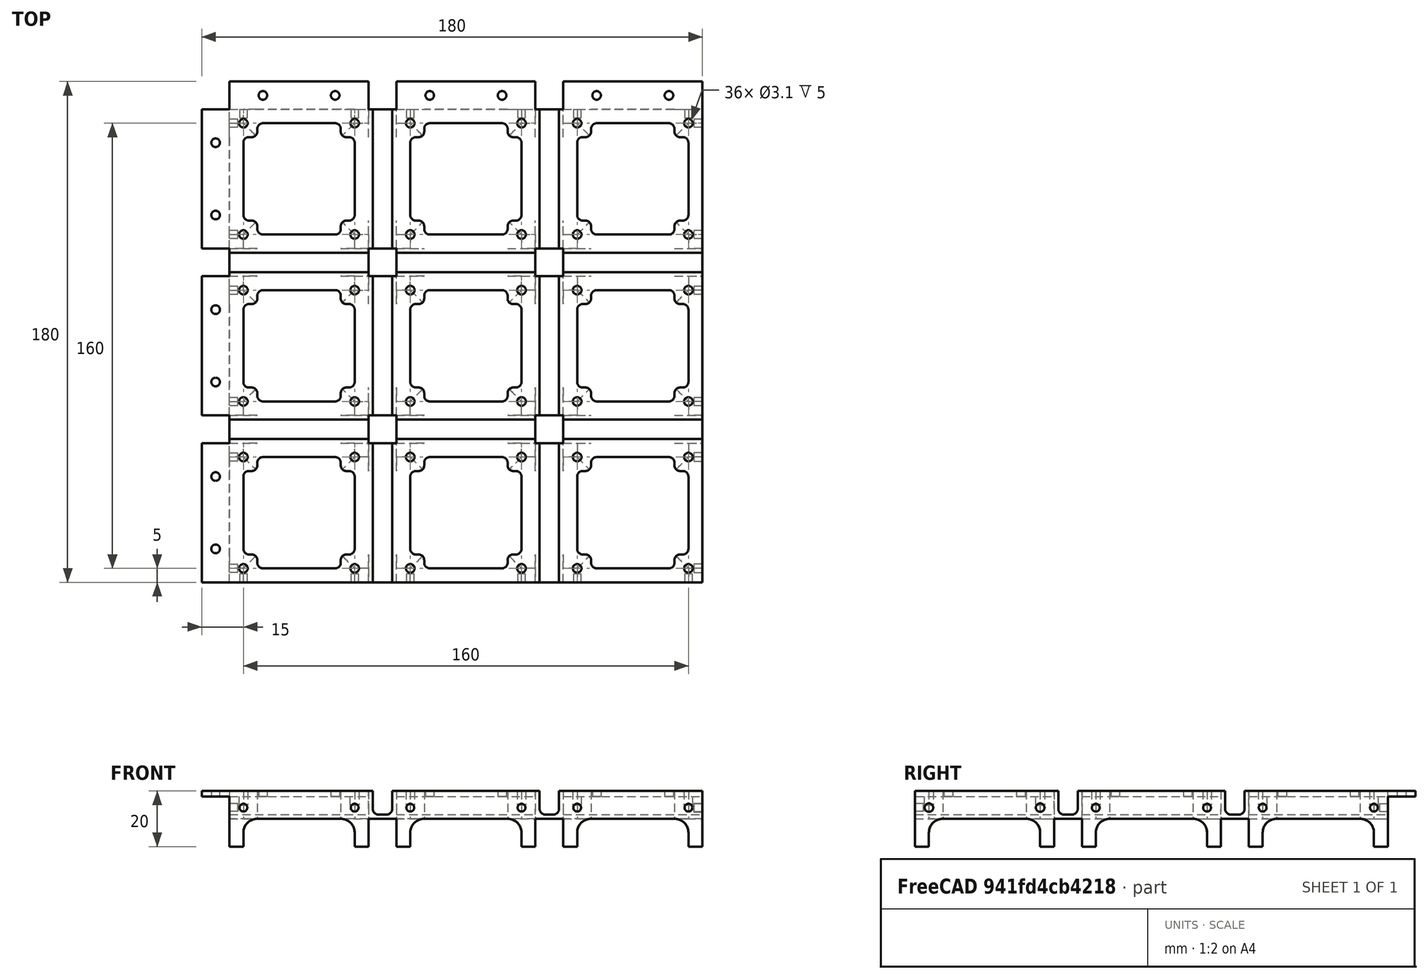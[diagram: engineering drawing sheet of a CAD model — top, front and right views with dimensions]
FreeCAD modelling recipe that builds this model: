
FCSTD DOCUMENT  (FreeCAD 0.20R29603 (Git))
Label: BackplaneRight
License: All rights reserved
LicenseURL: http://en.wikipedia.org/wiki/All_rights_reserved
objects: Sketcher::SketchObject×59, PartDesign::Pocket×49, App::Link×16, PartDesign::Pad×10, PartDesign::Body×10, Part::Cylinder×2, Part::Cut×2, Part::Box×1, App::Part×1, Part::MultiFuse×1, Mesh::Feature×1
note: 193 computed .brp shape members not serialized (recipe doc carries the construction recipe); baked Part::Feature solids carry a one-line shape summary decoded from their .brp

FEATURE [Sketcher::SketchObject] Sketch
  FullyConstrained = true
  MapMode = 5
  Placement = pos=(0,0,0) rot=(0.57735,0.57735,0.57735;2.0944rad)
  Support = -> [YZ_Plane001]
  sketch-geometry (4):
    g0: LineSegment StartX=0 StartY=0 StartZ=0 EndX=10 EndY=0 EndZ=0
    g1: LineSegment StartX=10 StartY=0 StartZ=0 EndX=10 EndY=10 EndZ=0
    g2: LineSegment StartX=10 StartY=10 StartZ=0 EndX=0 EndY=10 EndZ=0
    g3: LineSegment StartX=0 StartY=10 StartZ=0 EndX=0 EndY=0 EndZ=0
  constraints (11):
    c: Coincident(g0,g1)
    c: Coincident(g1,g2)
    c: Coincident(g2,g3)
    c: Coincident(g3,g0)
    c: Horizontal(g0)
    c: Horizontal(g2)
    c: Vertical(g1)
    c: Vertical(g3)
    c: Coincident(g0,g-1)
    c: DistanceY(g3,g3) = 10
    c: DistanceX(g2,g2) = 10
FEATURE [PartDesign::Pad] Pad
  Direction = (1,-2e-16,3e-16)
  Length = 50
  Length2 = 10
  Placement = pos=(0,0,0) rot=(0.57735,0.57735,0.57735;2.0944rad)
  Profile = -> Sketch
  ReferenceAxis = -> Sketch [N_Axis]
  Type = 0
FEATURE [Sketcher::SketchObject] Sketch001
  ExternalGeometry = -> [Pad]
  FullyConstrained = true
  MapMode = 5
  Placement = pos=(0,0,0) rot=(0.57735,0.57735,-0.57735;4.18879rad)
  Support = -> [Pad]
  sketch-geometry (6):
    g0: LineSegment StartX=8.5 StartY=-10 StartZ=0 EndX=8.5 EndY=-3.5 EndZ=0
    g1: LineSegment StartX=6.5 StartY=-1.5 StartZ=0 EndX=3.5 EndY=-1.5 EndZ=0
    g2: LineSegment StartX=1.5 StartY=-3.5 StartZ=0 EndX=1.5 EndY=-10 EndZ=0
    g3: ArcOfCircle CenterX=6.5 CenterY=-3.5 CenterZ=0 NormalX=0 NormalY=0 NormalZ=1 AngleXU=0 Radius=2 StartAngle=1e-16 EndAngle=1.5708
    g4: ArcOfCircle CenterX=3.5 CenterY=-3.5 CenterZ=0 NormalX=0 NormalY=0 NormalZ=1 AngleXU=0 Radius=2 StartAngle=1.5708 EndAngle=3.14159
    g5: LineSegment StartX=1.5 StartY=-10 StartZ=0 EndX=8.5 EndY=-10 EndZ=0
  constraints (16):
    c: PointOnObject(g0,g-3)
    c: Vertical(g0)
    c: Horizontal(g1)
    c: PointOnObject(g2,g-3)
    c: Vertical(g2)
    c: Tangent(g0,g3) = -1.5708
    c: Tangent(g1,g3) = -1.5708
    c: Tangent(g1,g4) = -1.5708
    c: Tangent(g2,g4) = -1.5708
    c: Radius(g4) = 2
    c: Radius(g3) = 2
    c: Distance(g2,g-5) = 1.5
    c: Distance(g0,g-4) = 1.5
    c: Distance(g1,g-6) = 1.5
    c: Coincident(g5,g2)
    c: Coincident(g5,g0)
FEATURE [PartDesign::Pocket] Pocket
  BaseFeature = -> Pad
  Direction = (1,-4e-16,4e-16)
  Length = 5
  Length2 = 5
  Placement = pos=(0,0,0) rot=(0.57735,0.57735,0.57735;2.0944rad)
  Profile = -> Sketch001
  ReferenceAxis = -> Sketch001 [N_Axis]
  Type = 1
FEATURE [PartDesign::Body] Body  label="BackplaneChannel"
  Group = -> [Sketch,Pad,Sketch001,Pocket]
  Origin = -> Origin001
  Placement = pos=(0,50,10) rot=(0,0,1;0rad)
  Tip = -> Pocket
FEATURE [App::Link] Link008  label="BackplaneChannel001"
  LinkPlacement = pos=(60,50,10) rot=(0,0,1;0rad)
  LinkedObject = -> Body
  Placement = pos=(60,50,10) rot=(0,0,1;0rad)
FEATURE [App::Link] Link009  label="BackplaneChannel002"
  LinkPlacement = pos=(120,50,10) rot=(0,0,1;0rad)
  LinkedObject = -> Body
  Placement = pos=(120,50,10) rot=(0,0,1;0rad)
FEATURE [App::Link] Link010  label="BackplaneChannel003"
  LinkPlacement = pos=(0,110,10) rot=(0,0,1;0rad)
  LinkedObject = -> Body
  Placement = pos=(0,110,10) rot=(0,0,1;0rad)
FEATURE [App::Link] Link011  label="BackplaneChannel004"
  LinkPlacement = pos=(60,110,10) rot=(0,0,1;0rad)
  LinkedObject = -> Body
  Placement = pos=(60,110,10) rot=(0,0,1;0rad)
FEATURE [App::Link] Link012  label="BackplaneChannel005"
  LinkPlacement = pos=(120,110,10) rot=(0,0,1;0rad)
  LinkedObject = -> Body
  Placement = pos=(120,110,10) rot=(0,0,1;0rad)
FEATURE [App::Link] Link013  label="BackplaneChannel006"
  LinkPlacement = pos=(60,0,10) rot=(0,0,1;1.5708rad)
  LinkedObject = -> Body
  Placement = pos=(60,0,10) rot=(0,0,1;1.5708rad)
FEATURE [App::Link] Link014  label="BackplaneChannel007"
  LinkPlacement = pos=(120,0,10) rot=(0,0,1;1.5708rad)
  LinkedObject = -> Body
  Placement = pos=(120,0,10) rot=(0,0,1;1.5708rad)
FEATURE [App::Link] Link015  label="BackplaneChannel008"
  LinkPlacement = pos=(60,60,10) rot=(0,0,1;1.5708rad)
  LinkedObject = -> Body
  Placement = pos=(60,60,10) rot=(0,0,1;1.5708rad)
FEATURE [App::Link] Link016  label="BackplaneChannel009"
  LinkPlacement = pos=(60,120,10) rot=(0,0,1;1.5708rad)
  LinkedObject = -> Body
  Placement = pos=(60,120,10) rot=(0,0,1;1.5708rad)
FEATURE [App::Link] Link017  label="BackplaneChannel010"
  LinkPlacement = pos=(120,60,10) rot=(0,0,1;1.5708rad)
  LinkedObject = -> Body
  Placement = pos=(120,60,10) rot=(0,0,1;1.5708rad)
FEATURE [App::Link] Link018  label="BackplaneChannel011"
  LinkPlacement = pos=(120,120,10) rot=(0,0,1;1.5708rad)
  LinkedObject = -> Body
  Placement = pos=(120,120,10) rot=(0,0,1;1.5708rad)
FEATURE [Sketcher::SketchObject] Sketch002
  FullyConstrained = true
  MapMode = 5
  Support = -> [XY_Plane002]
  sketch-geometry (4):
    g0: LineSegment StartX=-25 StartY=25 StartZ=0 EndX=25 EndY=25 EndZ=0
    g1: LineSegment StartX=25 StartY=25 StartZ=0 EndX=25 EndY=-25 EndZ=0
    g2: LineSegment StartX=25 StartY=-25 StartZ=0 EndX=-25 EndY=-25 EndZ=0
    g3: LineSegment StartX=-25 StartY=-25 StartZ=0 EndX=-25 EndY=25 EndZ=0
  constraints (10):
    c: Coincident(g0,g1)
    c: Coincident(g1,g2)
    c: Coincident(g2,g3)
    c: Coincident(g3,g0)
    c: Horizontal(g0)
    c: Vertical(g3)
    c: Symmetric(g2,g1,g-2)
    c: Symmetric(g1,g0,g-1)
    c: DistanceY(g1,g1) = 50
    c: DistanceX(g2,g2) = 50
FEATURE [PartDesign::Pad] Pad001
  Direction = (0,0,1)
  Length = 20
  Length2 = 10
  Profile = -> Sketch002
  ReferenceAxis = -> Sketch002 [N_Axis]
  Type = 0
FEATURE [Sketcher::SketchObject] Sketch003
  ExternalGeometry = -> [Pad001]
  FullyConstrained = true
  MapMode = 5
  Placement = pos=(0,0,20) rot=(0,0,1;0rad)
  Support = -> [Pad001]
  sketch-geometry (36):
    g0: LineSegment StartX=-18 StartY=15 StartZ=0 EndX=-17 EndY=15 EndZ=0
    g1: LineSegment StartX=20 StartY=13 StartZ=0 EndX=20 EndY=-13 EndZ=0
    g2: LineSegment StartX=18 StartY=-15 StartZ=0 EndX=17 EndY=-15 EndZ=0
    g3: LineSegment StartX=-20 StartY=-13 StartZ=0 EndX=-20 EndY=13 EndZ=0
    g4: LineSegment StartX=-13 StartY=20 StartZ=0 EndX=13 EndY=20 EndZ=0
    g5: LineSegment StartX=15 StartY=18 StartZ=0 EndX=15 EndY=17 EndZ=0
    g6: LineSegment StartX=13 StartY=-20 StartZ=0 EndX=-13 EndY=-20 EndZ=0
    g7: LineSegment StartX=-15 StartY=-18 StartZ=0 EndX=-15 EndY=-17 EndZ=0
    g8: LineSegment StartX=17 StartY=15 StartZ=0 EndX=18 EndY=15 EndZ=0
    g9: LineSegment StartX=-15 StartY=17 StartZ=0 EndX=-15 EndY=18 EndZ=0
    g10: LineSegment StartX=-17 StartY=-15 StartZ=0 EndX=-18 EndY=-15 EndZ=0
    g11: LineSegment StartX=15 StartY=-17 StartZ=0 EndX=15 EndY=-18 EndZ=0
    g12: ArcOfCircle CenterX=-13 CenterY=-18 CenterZ=0 NormalX=0 NormalY=0 NormalZ=1 AngleXU=0 Radius=2 StartAngle=3.14159 EndAngle=4.71239
    g13: GeomPoint X=-15 Y=-20 Z=0
    g14: ArcOfCircle CenterX=13 CenterY=-18 CenterZ=0 NormalX=0 NormalY=0 NormalZ=1 AngleXU=0 Radius=2 StartAngle=4.71239 EndAngle=6.28319
    g15: GeomPoint X=15 Y=-20 Z=0
    g16: ArcOfCircle CenterX=17 CenterY=-17 CenterZ=0 NormalX=0 NormalY=0 NormalZ=1 AngleXU=0 Radius=2 StartAngle=1.5708 EndAngle=3.14159
    g17: GeomPoint X=15 Y=-15 Z=0
    g18: ArcOfCircle CenterX=18 CenterY=-13 CenterZ=0 NormalX=0 NormalY=0 NormalZ=1 AngleXU=0 Radius=2 StartAngle=4.71239 EndAngle=6.28319
    g19: GeomPoint X=20 Y=-15 Z=0
    g20: ArcOfCircle CenterX=18 CenterY=13 CenterZ=0 NormalX=0 NormalY=0 NormalZ=1 AngleXU=0 Radius=2 StartAngle=0 EndAngle=1.5708
    g21: GeomPoint X=20 Y=15 Z=0
    g22: ArcOfCircle CenterX=17 CenterY=17 CenterZ=0 NormalX=0 NormalY=0 NormalZ=1 AngleXU=0 Radius=2 StartAngle=3.14159 EndAngle=4.71239
    g23: GeomPoint X=15 Y=15 Z=0
    g24: ArcOfCircle CenterX=13 CenterY=18 CenterZ=0 NormalX=0 NormalY=0 NormalZ=1 AngleXU=0 Radius=2 StartAngle=4e-16 EndAngle=1.5708
    g25: GeomPoint X=15 Y=20 Z=0
    g26: ArcOfCircle CenterX=-13 CenterY=18 CenterZ=0 NormalX=0 NormalY=0 NormalZ=1 AngleXU=0 Radius=2 StartAngle=1.5708 EndAngle=3.14159
    g27: GeomPoint X=-15 Y=20 Z=0
    g28: ArcOfCircle CenterX=-17 CenterY=17 CenterZ=0 NormalX=0 NormalY=0 NormalZ=1 AngleXU=0 Radius=2 StartAngle=4.71239 EndAngle=6.28319
    g29: GeomPoint X=-15 Y=15 Z=0
    g30: ArcOfCircle CenterX=-18 CenterY=13 CenterZ=0 NormalX=0 NormalY=0 NormalZ=1 AngleXU=0 Radius=2 StartAngle=1.5708 EndAngle=3.14159
    g31: GeomPoint X=-20 Y=15 Z=0
    g32: ArcOfCircle CenterX=-18 CenterY=-13 CenterZ=0 NormalX=0 NormalY=0 NormalZ=1 AngleXU=0 Radius=2 StartAngle=3.14159 EndAngle=4.71239
    g33: GeomPoint X=-20 Y=-15 Z=0
    g34: ArcOfCircle CenterX=-17 CenterY=-17 CenterZ=0 NormalX=0 NormalY=0 NormalZ=1 AngleXU=0 Radius=2 StartAngle=0 EndAngle=1.5708
    g35: GeomPoint X=-15 Y=-15 Z=0
  constraints (80):
    c: Horizontal(g2)
    c: Vertical(g3)
    c: Symmetric(g21,g31,g-2)
    c: Symmetric(g21,g19,g-1)
    c: DistanceX(g31,g21) = 40
    c: DistanceY(g19,g21) = 30
    c: Horizontal(g4)
    c: Vertical(g7)
    c: Symmetric(g13,g15,g-2)
    c: Symmetric(g15,g25,g-1)
    c: DistanceY(g15,g25) = 40
    c: Vertical(g9)
    c: Vertical(g5)
    c: Vertical(g11)
    c: Horizontal(g10)
    c: Horizontal(g8)
    c: Horizontal(g0)
    c: DistanceX(g13,g15) = 30
    c: DistanceY(g33,g31) = 30
    c: DistanceX(g27,g25) = 30
    c: PointOnObject(g13,g7)
    c: PointOnObject(g13,g6)
    c: Tangent(g7,g12) = 1.5708
    c: Tangent(g6,g12) = 1.5708
    c: Radius(g12) = 2
    c: PointOnObject(g15,g11)
    c: PointOnObject(g15,g6)
    c: Tangent(g11,g14) = 1.5708
    c: Tangent(g6,g14) = 1.5708
    c: PointOnObject(g17,g11)
    c: PointOnObject(g17,g2)
    c: Tangent(g11,g16) = -1.5708
    c: Tangent(g2,g16) = -1.5708
    c: PointOnObject(g19,g2)
    c: PointOnObject(g19,g1)
    c: Tangent(g2,g18) = 1.5708
    c: Tangent(g1,g18) = 1.5708
    c: PointOnObject(g21,g1)
    c: PointOnObject(g21,g8)
    c: Tangent(g1,g20) = 1.5708
    c: Tangent(g8,g20) = 1.5708
    c: PointOnObject(g23,g8)
    c: PointOnObject(g23,g5)
    c: Tangent(g8,g22) = -1.5708
    c: Tangent(g5,g22) = -1.5708
    c: PointOnObject(g25,g5)
    c: PointOnObject(g25,g4)
    c: Tangent(g5,g24) = 1.5708
    c: Tangent(g4,g24) = 1.5708
    c: PointOnObject(g27,g9)
    c: PointOnObject(g27,g4)
    c: Tangent(g9,g26) = 1.5708
    c: Tangent(g4,g26) = 1.5708
    c: PointOnObject(g29,g9)
    c: PointOnObject(g29,g0)
    c: Tangent(g9,g28) = -1.5708
    c: Tangent(g0,g28) = -1.5708
    c: PointOnObject(g31,g0)
    c: PointOnObject(g31,g3)
    c: Tangent(g0,g30) = 1.5708
    c: Tangent(g3,g30) = 1.5708
    c: PointOnObject(g33,g3)
    c: PointOnObject(g33,g10)
    c: Tangent(g3,g32) = 1.5708
    c: Tangent(g10,g32) = 1.5708
    c: PointOnObject(g35,g10)
    c: PointOnObject(g35,g7)
    c: Tangent(g10,g34) = -1.5708
    c: Tangent(g7,g34) = -1.5708
    c: Radius(g34) = 2
    c: Radius(g32) = 2
    c: Radius(g30) = 2
    c: Radius(g28) = 2
    c: Radius(g26) = 2
    c: Radius(g24) = 2
    c: Radius(g22) = 2
    c: Radius(g20) = 2
    c: Radius(g18) = 2
    c: Radius(g16) = 2
    c: Radius(g14) = 2
FEATURE [PartDesign::Pocket] Pocket001
  BaseFeature = -> Pad001
  Direction = (0,0,-1)
  Length = 5
  Length2 = 5
  Profile = -> Sketch003
  ReferenceAxis = -> Sketch003 [N_Axis]
  Type = 1
FEATURE [Sketcher::SketchObject] Sketch004
  ExternalGeometry = -> [Pocket001]
  FullyConstrained = true
  MapMode = 5
  Placement = pos=(25,0,0) rot=(0.57735,0.57735,0.57735;2.0944rad)
  Support = -> [Pocket001]
  sketch-geometry (6):
    g0: LineSegment StartX=-15 StartY=10 StartZ=0 EndX=15 EndY=10 EndZ=0
    g1: LineSegment StartX=20 StartY=5 StartZ=0 EndX=20 EndY=0 EndZ=0
    g2: LineSegment StartX=20 StartY=0 StartZ=0 EndX=-20 EndY=0 EndZ=0
    g3: LineSegment StartX=-20 StartY=0 StartZ=0 EndX=-20 EndY=5 EndZ=0
    g4: ArcOfCircle CenterX=15 CenterY=5 CenterZ=0 NormalX=0 NormalY=0 NormalZ=1 AngleXU=0 Radius=5 StartAngle=1.11001e-11 EndAngle=1.5708
    g5: ArcOfCircle CenterX=-15 CenterY=5 CenterZ=0 NormalX=0 NormalY=0 NormalZ=1 AngleXU=0 Radius=5 StartAngle=1.5708 EndAngle=3.14159
  constraints (15):
    c: Coincident(g1,g2)
    c: Coincident(g2,g3)
    c: Vertical(g1)
    c: Vertical(g3)
    c: PointOnObject(g1,g-1)
    c: Tangent(g1,g4) = 1.5708
    c: Tangent(g0,g4) = 1.5708
    c: Tangent(g0,g5) = 1.5708
    c: Tangent(g3,g5) = 1.5708
    c: Horizontal(g0)
    c: DistanceX(g2,g2) = 40
    c: Symmetric(g2,g1,g-2)
    c: Distance(g-1,g0) = 10
    c: Radius(g5) = 5
    c: Radius(g4) = 5
FEATURE [PartDesign::Pocket] Pocket002
  BaseFeature = -> Pocket001
  Direction = (-1,0,0)
  Length = 5
  Length2 = 5
  Profile = -> Sketch004
  ReferenceAxis = -> Sketch004 [N_Axis]
  Type = 1
FEATURE [Sketcher::SketchObject] Sketch005
  FullyConstrained = true
  MapMode = 5
  Placement = pos=(0,-25,0) rot=(1,0,0;1.5708rad)
  Support = -> [Pocket001]
  sketch-geometry (6):
    g0: LineSegment StartX=-15 StartY=10 StartZ=0 EndX=15 EndY=10 EndZ=0
    g1: LineSegment StartX=20 StartY=5 StartZ=0 EndX=20 EndY=0 EndZ=0
    g2: LineSegment StartX=20 StartY=0 StartZ=0 EndX=-20 EndY=0 EndZ=0
    g3: LineSegment StartX=-20 StartY=0 StartZ=0 EndX=-20 EndY=5 EndZ=0
    g4: ArcOfCircle CenterX=15 CenterY=5 CenterZ=0 NormalX=0 NormalY=0 NormalZ=1 AngleXU=0 Radius=5 StartAngle=1.11e-11 EndAngle=1.5708
    g5: ArcOfCircle CenterX=-15 CenterY=5 CenterZ=0 NormalX=0 NormalY=0 NormalZ=1 AngleXU=0 Radius=5 StartAngle=1.5708 EndAngle=3.14159
  constraints (15):
    c: Coincident(g1,g2)
    c: Coincident(g2,g3)
    c: Horizontal(g0)
    c: Vertical(g1)
    c: Vertical(g3)
    c: Symmetric(g2,g1,g-2)
    c: PointOnObject(g1,g-1)
    c: Tangent(g0,g4) = 1.5708
    c: Tangent(g1,g4) = 1.5708
    c: Tangent(g0,g5) = 1.5708
    c: Tangent(g3,g5) = 1.5708
    c: DistanceX(g2,g2) = 40
    c: Distance(g-1,g0) = 10
    c: Radius(g5) = 5
    c: Radius(g4) = 5
FEATURE [PartDesign::Pocket] Pocket003
  BaseFeature = -> Pocket002
  Direction = (0,1,-2e-16)
  Length = 5
  Length2 = 5
  Profile = -> Sketch005
  ReferenceAxis = -> Sketch005 [N_Axis]
  Type = 1
FEATURE [Sketcher::SketchObject] Sketch009
  FullyConstrained = false
  MapMode = 5
  Placement = pos=(0,0,20) rot=(0,0,1;0rad)
  sketch-geometry (4):
    g0: Circle CenterX=-20 CenterY=20 CenterZ=0 NormalX=0 NormalY=0 NormalZ=1 AngleXU=0 Radius=1.55
    g1: Circle CenterX=20 CenterY=20 CenterZ=0 NormalX=0 NormalY=0 NormalZ=1 AngleXU=0 Radius=1.55
    g2: Circle CenterX=20 CenterY=-20 CenterZ=0 NormalX=0 NormalY=0 NormalZ=1 AngleXU=0 Radius=1.55
    g3: Circle CenterX=-20 CenterY=-20 CenterZ=0 NormalX=0 NormalY=0 NormalZ=1 AngleXU=0 Radius=1.55
  constraints (4):
    c: Diameter(g0) = 3.1
    c: Diameter(g1) = 3.1
    c: Diameter(g2) = 3.1
    c: Diameter(g3) = 3.1
FEATURE [PartDesign::Pocket] Pocket008
  BaseFeature = -> Pocket003
  Direction = (0,0,-1)
  Length = 5
  Length2 = 5
  Profile = -> Sketch009
  ReferenceAxis = -> Sketch009 [N_Axis]
  Type = 0
FEATURE [Sketcher::SketchObject] Sketch010
  FullyConstrained = true
  MapMode = 5
  Support = -> [XY_Plane003]
  sketch-geometry (4):
    g0: LineSegment StartX=-25 StartY=25 StartZ=0 EndX=25 EndY=25 EndZ=0
    g1: LineSegment StartX=25 StartY=25 StartZ=0 EndX=25 EndY=-25 EndZ=0
    g2: LineSegment StartX=25 StartY=-25 StartZ=0 EndX=-25 EndY=-25 EndZ=0
    g3: LineSegment StartX=-25 StartY=-25 StartZ=0 EndX=-25 EndY=25 EndZ=0
  constraints (10):
    c: Coincident(g0,g1)
    c: Coincident(g1,g2)
    c: Coincident(g2,g3)
    c: Coincident(g3,g0)
    c: Horizontal(g0)
    c: Vertical(g3)
    c: Symmetric(g2,g1,g-2)
    c: Symmetric(g1,g0,g-1)
    c: DistanceY(g1,g1) = 50
    c: DistanceX(g2,g2) = 50
FEATURE [PartDesign::Pad] Pad002
  Direction = (0,0,1)
  Length = 20
  Length2 = 10
  Profile = -> Sketch010
  ReferenceAxis = -> Sketch010 [N_Axis]
  Type = 0
FEATURE [Sketcher::SketchObject] Sketch011
  ExternalGeometry = -> [Pad002]
  FullyConstrained = true
  MapMode = 5
  Placement = pos=(0,0,20) rot=(0,0,1;0rad)
  Support = -> [Pad002]
  sketch-geometry (36):
    g0: LineSegment StartX=-18 StartY=15 StartZ=0 EndX=-17 EndY=15 EndZ=0
    g1: LineSegment StartX=20 StartY=13 StartZ=0 EndX=20 EndY=-13 EndZ=0
    g2: LineSegment StartX=18 StartY=-15 StartZ=0 EndX=17 EndY=-15 EndZ=0
    g3: LineSegment StartX=-20 StartY=-13 StartZ=0 EndX=-20 EndY=13 EndZ=0
    g4: LineSegment StartX=-13 StartY=20 StartZ=0 EndX=13 EndY=20 EndZ=0
    g5: LineSegment StartX=15 StartY=18 StartZ=0 EndX=15 EndY=17 EndZ=0
    g6: LineSegment StartX=13 StartY=-20 StartZ=0 EndX=-13 EndY=-20 EndZ=0
    g7: LineSegment StartX=-15 StartY=-18 StartZ=0 EndX=-15 EndY=-17 EndZ=0
    g8: LineSegment StartX=17 StartY=15 StartZ=0 EndX=18 EndY=15 EndZ=0
    g9: LineSegment StartX=-15 StartY=17 StartZ=0 EndX=-15 EndY=18 EndZ=0
    g10: LineSegment StartX=-17 StartY=-15 StartZ=0 EndX=-18 EndY=-15 EndZ=0
    g11: LineSegment StartX=15 StartY=-17 StartZ=0 EndX=15 EndY=-18 EndZ=0
    g12: ArcOfCircle CenterX=-13 CenterY=-18 CenterZ=0 NormalX=0 NormalY=0 NormalZ=1 AngleXU=0 Radius=2 StartAngle=3.14159 EndAngle=4.71239
    g13: GeomPoint X=-15 Y=-20 Z=0
    g14: ArcOfCircle CenterX=13 CenterY=-18 CenterZ=0 NormalX=0 NormalY=0 NormalZ=1 AngleXU=0 Radius=2 StartAngle=4.71239 EndAngle=6.28319
    g15: GeomPoint X=15 Y=-20 Z=0
    g16: ArcOfCircle CenterX=17 CenterY=-17 CenterZ=0 NormalX=0 NormalY=0 NormalZ=1 AngleXU=0 Radius=2 StartAngle=1.5708 EndAngle=3.14159
    g17: GeomPoint X=15 Y=-15 Z=0
    g18: ArcOfCircle CenterX=18 CenterY=-13 CenterZ=0 NormalX=0 NormalY=0 NormalZ=1 AngleXU=0 Radius=2 StartAngle=4.71239 EndAngle=6.28319
    g19: GeomPoint X=20 Y=-15 Z=0
    g20: ArcOfCircle CenterX=18 CenterY=13 CenterZ=0 NormalX=0 NormalY=0 NormalZ=1 AngleXU=0 Radius=2 StartAngle=0 EndAngle=1.5708
    g21: GeomPoint X=20 Y=15 Z=0
    g22: ArcOfCircle CenterX=17 CenterY=17 CenterZ=0 NormalX=0 NormalY=0 NormalZ=1 AngleXU=0 Radius=2 StartAngle=3.14159 EndAngle=4.71239
    g23: GeomPoint X=15 Y=15 Z=0
    g24: ArcOfCircle CenterX=13 CenterY=18 CenterZ=0 NormalX=0 NormalY=0 NormalZ=1 AngleXU=0 Radius=2 StartAngle=4e-16 EndAngle=1.5708
    g25: GeomPoint X=15 Y=20 Z=0
    g26: ArcOfCircle CenterX=-13 CenterY=18 CenterZ=0 NormalX=0 NormalY=0 NormalZ=1 AngleXU=0 Radius=2 StartAngle=1.5708 EndAngle=3.14159
    g27: GeomPoint X=-15 Y=20 Z=0
    g28: ArcOfCircle CenterX=-17 CenterY=17 CenterZ=0 NormalX=0 NormalY=0 NormalZ=1 AngleXU=0 Radius=2 StartAngle=4.71239 EndAngle=6.28319
    g29: GeomPoint X=-15 Y=15 Z=0
    g30: ArcOfCircle CenterX=-18 CenterY=13 CenterZ=0 NormalX=0 NormalY=0 NormalZ=1 AngleXU=0 Radius=2 StartAngle=1.5708 EndAngle=3.14159
    g31: GeomPoint X=-20 Y=15 Z=0
    g32: ArcOfCircle CenterX=-18 CenterY=-13 CenterZ=0 NormalX=0 NormalY=0 NormalZ=1 AngleXU=0 Radius=2 StartAngle=3.14159 EndAngle=4.71239
    g33: GeomPoint X=-20 Y=-15 Z=0
    g34: ArcOfCircle CenterX=-17 CenterY=-17 CenterZ=0 NormalX=0 NormalY=0 NormalZ=1 AngleXU=0 Radius=2 StartAngle=0 EndAngle=1.5708
    g35: GeomPoint X=-15 Y=-15 Z=0
  constraints (80):
    c: Horizontal(g2)
    c: Vertical(g3)
    c: Symmetric(g21,g31,g-2)
    c: Symmetric(g21,g19,g-1)
    c: DistanceX(g31,g21) = 40
    c: DistanceY(g19,g21) = 30
    c: Horizontal(g4)
    c: Vertical(g7)
    c: Symmetric(g13,g15,g-2)
    c: Symmetric(g15,g25,g-1)
    c: DistanceY(g15,g25) = 40
    c: Vertical(g9)
    c: Vertical(g5)
    c: Vertical(g11)
    c: Horizontal(g10)
    c: Horizontal(g8)
    c: Horizontal(g0)
    c: DistanceX(g13,g15) = 30
    c: DistanceY(g33,g31) = 30
    c: DistanceX(g27,g25) = 30
    c: PointOnObject(g13,g7)
    c: PointOnObject(g13,g6)
    c: Tangent(g7,g12) = 1.5708
    c: Tangent(g6,g12) = 1.5708
    c: Radius(g12) = 2
    c: PointOnObject(g15,g11)
    c: PointOnObject(g15,g6)
    c: Tangent(g11,g14) = 1.5708
    c: Tangent(g6,g14) = 1.5708
    c: PointOnObject(g17,g11)
    c: PointOnObject(g17,g2)
    c: Tangent(g11,g16) = -1.5708
    c: Tangent(g2,g16) = -1.5708
    c: PointOnObject(g19,g2)
    c: PointOnObject(g19,g1)
    c: Tangent(g2,g18) = 1.5708
    c: Tangent(g1,g18) = 1.5708
    c: PointOnObject(g21,g1)
    c: PointOnObject(g21,g8)
    c: Tangent(g1,g20) = 1.5708
    c: Tangent(g8,g20) = 1.5708
    c: PointOnObject(g23,g8)
    c: PointOnObject(g23,g5)
    c: Tangent(g8,g22) = -1.5708
    c: Tangent(g5,g22) = -1.5708
    c: PointOnObject(g25,g5)
    c: PointOnObject(g25,g4)
    c: Tangent(g5,g24) = 1.5708
    c: Tangent(g4,g24) = 1.5708
    c: PointOnObject(g27,g9)
    c: PointOnObject(g27,g4)
    c: Tangent(g9,g26) = 1.5708
    c: Tangent(g4,g26) = 1.5708
    c: PointOnObject(g29,g9)
    c: PointOnObject(g29,g0)
    c: Tangent(g9,g28) = -1.5708
    c: Tangent(g0,g28) = -1.5708
    c: PointOnObject(g31,g0)
    c: PointOnObject(g31,g3)
    c: Tangent(g0,g30) = 1.5708
    c: Tangent(g3,g30) = 1.5708
    c: PointOnObject(g33,g3)
    c: PointOnObject(g33,g10)
    c: Tangent(g3,g32) = 1.5708
    c: Tangent(g10,g32) = 1.5708
    c: PointOnObject(g35,g10)
    c: PointOnObject(g35,g7)
    c: Tangent(g10,g34) = -1.5708
    c: Tangent(g7,g34) = -1.5708
    c: Radius(g34) = 2
    c: Radius(g32) = 2
    c: Radius(g30) = 2
    c: Radius(g28) = 2
    c: Radius(g26) = 2
    c: Radius(g24) = 2
    c: Radius(g22) = 2
    c: Radius(g20) = 2
    c: Radius(g18) = 2
    c: Radius(g16) = 2
    c: Radius(g14) = 2
FEATURE [PartDesign::Pocket] Pocket009
  BaseFeature = -> Pad002
  Direction = (0,0,-1)
  Length = 5
  Length2 = 5
  Profile = -> Sketch011
  ReferenceAxis = -> Sketch011 [N_Axis]
  Type = 1
FEATURE [Sketcher::SketchObject] Sketch012
  ExternalGeometry = -> [Pocket009]
  FullyConstrained = true
  MapMode = 5
  Placement = pos=(25,0,0) rot=(0.57735,0.57735,0.57735;2.0944rad)
  Support = -> [Pocket009]
  sketch-geometry (6):
    g0: LineSegment StartX=-15 StartY=10 StartZ=0 EndX=15 EndY=10 EndZ=0
    g1: LineSegment StartX=20 StartY=5 StartZ=0 EndX=20 EndY=0 EndZ=0
    g2: LineSegment StartX=20 StartY=0 StartZ=0 EndX=-20 EndY=0 EndZ=0
    g3: LineSegment StartX=-20 StartY=0 StartZ=0 EndX=-20 EndY=5 EndZ=0
    g4: ArcOfCircle CenterX=15 CenterY=5 CenterZ=0 NormalX=0 NormalY=0 NormalZ=1 AngleXU=0 Radius=5 StartAngle=1.11001e-11 EndAngle=1.5708
    g5: ArcOfCircle CenterX=-15 CenterY=5 CenterZ=0 NormalX=0 NormalY=0 NormalZ=1 AngleXU=0 Radius=5 StartAngle=1.5708 EndAngle=3.14159
  constraints (15):
    c: Coincident(g1,g2)
    c: Coincident(g2,g3)
    c: Vertical(g1)
    c: Vertical(g3)
    c: PointOnObject(g1,g-1)
    c: Tangent(g1,g4) = 1.5708
    c: Tangent(g0,g4) = 1.5708
    c: Tangent(g0,g5) = 1.5708
    c: Tangent(g3,g5) = 1.5708
    c: Horizontal(g0)
    c: DistanceX(g2,g2) = 40
    c: Symmetric(g2,g1,g-2)
    c: Distance(g-1,g0) = 10
    c: Radius(g5) = 5
    c: Radius(g4) = 5
FEATURE [PartDesign::Pocket] Pocket010
  BaseFeature = -> Pocket009
  Direction = (-1,0,0)
  Length = 5
  Length2 = 5
  Profile = -> Sketch012
  ReferenceAxis = -> Sketch012 [N_Axis]
  Type = 1
FEATURE [Sketcher::SketchObject] Sketch013
  FullyConstrained = true
  MapMode = 5
  Placement = pos=(0,-25,0) rot=(1,0,0;1.5708rad)
  Support = -> [Pocket009]
  sketch-geometry (6):
    g0: LineSegment StartX=-15 StartY=10 StartZ=0 EndX=15 EndY=10 EndZ=0
    g1: LineSegment StartX=20 StartY=5 StartZ=0 EndX=20 EndY=0 EndZ=0
    g2: LineSegment StartX=20 StartY=0 StartZ=0 EndX=-20 EndY=0 EndZ=0
    g3: LineSegment StartX=-20 StartY=0 StartZ=0 EndX=-20 EndY=5 EndZ=0
    g4: ArcOfCircle CenterX=15 CenterY=5 CenterZ=0 NormalX=0 NormalY=0 NormalZ=1 AngleXU=0 Radius=5 StartAngle=1.11e-11 EndAngle=1.5708
    g5: ArcOfCircle CenterX=-15 CenterY=5 CenterZ=0 NormalX=0 NormalY=0 NormalZ=1 AngleXU=0 Radius=5 StartAngle=1.5708 EndAngle=3.14159
  constraints (15):
    c: Coincident(g1,g2)
    c: Coincident(g2,g3)
    c: Horizontal(g0)
    c: Vertical(g1)
    c: Vertical(g3)
    c: Symmetric(g2,g1,g-2)
    c: PointOnObject(g1,g-1)
    c: Tangent(g0,g4) = 1.5708
    c: Tangent(g1,g4) = 1.5708
    c: Tangent(g0,g5) = 1.5708
    c: Tangent(g3,g5) = 1.5708
    c: DistanceX(g2,g2) = 40
    c: Distance(g-1,g0) = 10
    c: Radius(g5) = 5
    c: Radius(g4) = 5
FEATURE [PartDesign::Pocket] Pocket011
  BaseFeature = -> Pocket010
  Direction = (0,1,-2e-16)
  Length = 5
  Length2 = 5
  Profile = -> Sketch013
  ReferenceAxis = -> Sketch013 [N_Axis]
  Type = 1
FEATURE [Sketcher::SketchObject] Sketch014
  FullyConstrained = false
  MapMode = 5
  Placement = pos=(0,0,20) rot=(0,0,1;0rad)
  sketch-geometry (4):
    g0: Circle CenterX=-20 CenterY=20 CenterZ=0 NormalX=0 NormalY=0 NormalZ=1 AngleXU=0 Radius=1.55
    g1: Circle CenterX=20 CenterY=20 CenterZ=0 NormalX=0 NormalY=0 NormalZ=1 AngleXU=0 Radius=1.55
    g2: Circle CenterX=20 CenterY=-20 CenterZ=0 NormalX=0 NormalY=0 NormalZ=1 AngleXU=0 Radius=1.55
    g3: Circle CenterX=-20 CenterY=-20 CenterZ=0 NormalX=0 NormalY=0 NormalZ=1 AngleXU=0 Radius=1.55
  constraints (4):
    c: Diameter(g0) = 3.1
    c: Diameter(g1) = 3.1
    c: Diameter(g2) = 3.1
    c: Diameter(g3) = 3.1
FEATURE [PartDesign::Pocket] Pocket012
  BaseFeature = -> Pocket011
  Direction = (0,0,-1)
  Length = 5
  Length2 = 5
  Profile = -> Sketch014
  ReferenceAxis = -> Sketch014 [N_Axis]
  Type = 0
FEATURE [PartDesign::Body] Body003  label="BackplaneBlock001"
  Group = -> [Sketch010,Pad002,Sketch011,Pocket009,Sketch012,Sketch013,Pocket010,Pocket011,Sketch014,Pocket012]
  Origin = -> Origin003
  Placement = pos=(85,85,0) rot=(0,0,1;0rad)
  Tip = -> Pocket012
FEATURE [Sketcher::SketchObject] Sketch015
  ExternalGeometry = -> [Pocket008]
  FullyConstrained = true
  MapMode = 5
  Placement = pos=(0,-25,0) rot=(1,0,0;1.5708rad)
  Support = -> [Pocket008]
  sketch-geometry (2):
    g0: Circle CenterX=-20 CenterY=14 CenterZ=0 NormalX=0 NormalY=0 NormalZ=1 AngleXU=0 Radius=1.4
    g1: Circle CenterX=20 CenterY=14 CenterZ=0 NormalX=0 NormalY=0 NormalZ=1 AngleXU=0 Radius=1.4
  constraints (6):
    c: Diameter(g0) = 2.8
    c: Diameter(g1) = 2.8
    c: Distance(g0,g-5) = 5
    c: Distance(g0,g-3) = 6
    c: Distance(g1,g-3) = 6
    c: Distance(g1,g-4) = 5
FEATURE [PartDesign::Pocket] Pocket013
  BaseFeature = -> Pocket008
  Direction = (0,1,-2e-16)
  Length = 3
  Length2 = 5
  Profile = -> Sketch015
  ReferenceAxis = -> Sketch015 [N_Axis]
  Type = 0
FEATURE [Sketcher::SketchObject] Sketch016
  FullyConstrained = true
  MapMode = 5
  Support = -> [XY_Plane004]
  sketch-geometry (4):
    g0: LineSegment StartX=-25 StartY=25 StartZ=0 EndX=25 EndY=25 EndZ=0
    g1: LineSegment StartX=25 StartY=25 StartZ=0 EndX=25 EndY=-25 EndZ=0
    g2: LineSegment StartX=25 StartY=-25 StartZ=0 EndX=-25 EndY=-25 EndZ=0
    g3: LineSegment StartX=-25 StartY=-25 StartZ=0 EndX=-25 EndY=25 EndZ=0
  constraints (10):
    c: Coincident(g0,g1)
    c: Coincident(g1,g2)
    c: Coincident(g2,g3)
    c: Coincident(g3,g0)
    c: Horizontal(g0)
    c: Vertical(g3)
    c: Symmetric(g2,g1,g-2)
    c: Symmetric(g1,g0,g-1)
    c: DistanceY(g1,g1) = 50
    c: DistanceX(g2,g2) = 50
FEATURE [PartDesign::Pad] Pad003
  Direction = (0,0,1)
  Length = 20
  Length2 = 10
  Profile = -> Sketch016
  ReferenceAxis = -> Sketch016 [N_Axis]
  Type = 0
FEATURE [Sketcher::SketchObject] Sketch017
  ExternalGeometry = -> [Pad003]
  FullyConstrained = true
  MapMode = 5
  Placement = pos=(0,0,20) rot=(0,0,1;0rad)
  Support = -> [Pad003]
  sketch-geometry (36):
    g0: LineSegment StartX=-18 StartY=15 StartZ=0 EndX=-17 EndY=15 EndZ=0
    g1: LineSegment StartX=20 StartY=13 StartZ=0 EndX=20 EndY=-13 EndZ=0
    g2: LineSegment StartX=18 StartY=-15 StartZ=0 EndX=17 EndY=-15 EndZ=0
    g3: LineSegment StartX=-20 StartY=-13 StartZ=0 EndX=-20 EndY=13 EndZ=0
    g4: LineSegment StartX=-13 StartY=20 StartZ=0 EndX=13 EndY=20 EndZ=0
    g5: LineSegment StartX=15 StartY=18 StartZ=0 EndX=15 EndY=17 EndZ=0
    g6: LineSegment StartX=13 StartY=-20 StartZ=0 EndX=-13 EndY=-20 EndZ=0
    g7: LineSegment StartX=-15 StartY=-18 StartZ=0 EndX=-15 EndY=-17 EndZ=0
    g8: LineSegment StartX=17 StartY=15 StartZ=0 EndX=18 EndY=15 EndZ=0
    g9: LineSegment StartX=-15 StartY=17 StartZ=0 EndX=-15 EndY=18 EndZ=0
    g10: LineSegment StartX=-17 StartY=-15 StartZ=0 EndX=-18 EndY=-15 EndZ=0
    g11: LineSegment StartX=15 StartY=-17 StartZ=0 EndX=15 EndY=-18 EndZ=0
    g12: ArcOfCircle CenterX=-13 CenterY=-18 CenterZ=0 NormalX=0 NormalY=0 NormalZ=1 AngleXU=0 Radius=2 StartAngle=3.14159 EndAngle=4.71239
    g13: GeomPoint X=-15 Y=-20 Z=0
    g14: ArcOfCircle CenterX=13 CenterY=-18 CenterZ=0 NormalX=0 NormalY=0 NormalZ=1 AngleXU=0 Radius=2 StartAngle=4.71239 EndAngle=6.28319
    g15: GeomPoint X=15 Y=-20 Z=0
    g16: ArcOfCircle CenterX=17 CenterY=-17 CenterZ=0 NormalX=0 NormalY=0 NormalZ=1 AngleXU=0 Radius=2 StartAngle=1.5708 EndAngle=3.14159
    g17: GeomPoint X=15 Y=-15 Z=0
    g18: ArcOfCircle CenterX=18 CenterY=-13 CenterZ=0 NormalX=0 NormalY=0 NormalZ=1 AngleXU=0 Radius=2 StartAngle=4.71239 EndAngle=6.28319
    g19: GeomPoint X=20 Y=-15 Z=0
    g20: ArcOfCircle CenterX=18 CenterY=13 CenterZ=0 NormalX=0 NormalY=0 NormalZ=1 AngleXU=0 Radius=2 StartAngle=0 EndAngle=1.5708
    g21: GeomPoint X=20 Y=15 Z=0
    g22: ArcOfCircle CenterX=17 CenterY=17 CenterZ=0 NormalX=0 NormalY=0 NormalZ=1 AngleXU=0 Radius=2 StartAngle=3.14159 EndAngle=4.71239
    g23: GeomPoint X=15 Y=15 Z=0
    g24: ArcOfCircle CenterX=13 CenterY=18 CenterZ=0 NormalX=0 NormalY=0 NormalZ=1 AngleXU=0 Radius=2 StartAngle=4e-16 EndAngle=1.5708
    g25: GeomPoint X=15 Y=20 Z=0
    g26: ArcOfCircle CenterX=-13 CenterY=18 CenterZ=0 NormalX=0 NormalY=0 NormalZ=1 AngleXU=0 Radius=2 StartAngle=1.5708 EndAngle=3.14159
    g27: GeomPoint X=-15 Y=20 Z=0
    g28: ArcOfCircle CenterX=-17 CenterY=17 CenterZ=0 NormalX=0 NormalY=0 NormalZ=1 AngleXU=0 Radius=2 StartAngle=4.71239 EndAngle=6.28319
    g29: GeomPoint X=-15 Y=15 Z=0
    g30: ArcOfCircle CenterX=-18 CenterY=13 CenterZ=0 NormalX=0 NormalY=0 NormalZ=1 AngleXU=0 Radius=2 StartAngle=1.5708 EndAngle=3.14159
    g31: GeomPoint X=-20 Y=15 Z=0
    g32: ArcOfCircle CenterX=-18 CenterY=-13 CenterZ=0 NormalX=0 NormalY=0 NormalZ=1 AngleXU=0 Radius=2 StartAngle=3.14159 EndAngle=4.71239
    g33: GeomPoint X=-20 Y=-15 Z=0
    g34: ArcOfCircle CenterX=-17 CenterY=-17 CenterZ=0 NormalX=0 NormalY=0 NormalZ=1 AngleXU=0 Radius=2 StartAngle=0 EndAngle=1.5708
    g35: GeomPoint X=-15 Y=-15 Z=0
  constraints (80):
    c: Horizontal(g2)
    c: Vertical(g3)
    c: Symmetric(g21,g31,g-2)
    c: Symmetric(g21,g19,g-1)
    c: DistanceX(g31,g21) = 40
    c: DistanceY(g19,g21) = 30
    c: Horizontal(g4)
    c: Vertical(g7)
    c: Symmetric(g13,g15,g-2)
    c: Symmetric(g15,g25,g-1)
    c: DistanceY(g15,g25) = 40
    c: Vertical(g9)
    c: Vertical(g5)
    c: Vertical(g11)
    c: Horizontal(g10)
    c: Horizontal(g8)
    c: Horizontal(g0)
    c: DistanceX(g13,g15) = 30
    c: DistanceY(g33,g31) = 30
    c: DistanceX(g27,g25) = 30
    c: PointOnObject(g13,g7)
    c: PointOnObject(g13,g6)
    c: Tangent(g7,g12) = 1.5708
    c: Tangent(g6,g12) = 1.5708
    c: Radius(g12) = 2
    c: PointOnObject(g15,g11)
    c: PointOnObject(g15,g6)
    c: Tangent(g11,g14) = 1.5708
    c: Tangent(g6,g14) = 1.5708
    c: PointOnObject(g17,g11)
    c: PointOnObject(g17,g2)
    c: Tangent(g11,g16) = -1.5708
    c: Tangent(g2,g16) = -1.5708
    c: PointOnObject(g19,g2)
    c: PointOnObject(g19,g1)
    c: Tangent(g2,g18) = 1.5708
    c: Tangent(g1,g18) = 1.5708
    c: PointOnObject(g21,g1)
    c: PointOnObject(g21,g8)
    c: Tangent(g1,g20) = 1.5708
    c: Tangent(g8,g20) = 1.5708
    c: PointOnObject(g23,g8)
    c: PointOnObject(g23,g5)
    c: Tangent(g8,g22) = -1.5708
    c: Tangent(g5,g22) = -1.5708
    c: PointOnObject(g25,g5)
    c: PointOnObject(g25,g4)
    c: Tangent(g5,g24) = 1.5708
    c: Tangent(g4,g24) = 1.5708
    c: PointOnObject(g27,g9)
    c: PointOnObject(g27,g4)
    c: Tangent(g9,g26) = 1.5708
    c: Tangent(g4,g26) = 1.5708
    c: PointOnObject(g29,g9)
    c: PointOnObject(g29,g0)
    c: Tangent(g9,g28) = -1.5708
    c: Tangent(g0,g28) = -1.5708
    c: PointOnObject(g31,g0)
    c: PointOnObject(g31,g3)
    c: Tangent(g0,g30) = 1.5708
    c: Tangent(g3,g30) = 1.5708
    c: PointOnObject(g33,g3)
    c: PointOnObject(g33,g10)
    c: Tangent(g3,g32) = 1.5708
    c: Tangent(g10,g32) = 1.5708
    c: PointOnObject(g35,g10)
    c: PointOnObject(g35,g7)
    c: Tangent(g10,g34) = -1.5708
    c: Tangent(g7,g34) = -1.5708
    c: Radius(g34) = 2
    c: Radius(g32) = 2
    c: Radius(g30) = 2
    c: Radius(g28) = 2
    c: Radius(g26) = 2
    c: Radius(g24) = 2
    c: Radius(g22) = 2
    c: Radius(g20) = 2
    c: Radius(g18) = 2
    c: Radius(g16) = 2
    c: Radius(g14) = 2
FEATURE [PartDesign::Pocket] Pocket014
  BaseFeature = -> Pad003
  Direction = (0,0,-1)
  Length = 5
  Length2 = 5
  Profile = -> Sketch017
  ReferenceAxis = -> Sketch017 [N_Axis]
  Type = 1
FEATURE [Sketcher::SketchObject] Sketch018
  ExternalGeometry = -> [Pocket014]
  FullyConstrained = true
  MapMode = 5
  Placement = pos=(25,0,0) rot=(0.57735,0.57735,0.57735;2.0944rad)
  Support = -> [Pocket014]
  sketch-geometry (6):
    g0: LineSegment StartX=-15 StartY=10 StartZ=0 EndX=15 EndY=10 EndZ=0
    g1: LineSegment StartX=20 StartY=5 StartZ=0 EndX=20 EndY=0 EndZ=0
    g2: LineSegment StartX=20 StartY=0 StartZ=0 EndX=-20 EndY=0 EndZ=0
    g3: LineSegment StartX=-20 StartY=0 StartZ=0 EndX=-20 EndY=5 EndZ=0
    g4: ArcOfCircle CenterX=15 CenterY=5 CenterZ=0 NormalX=0 NormalY=0 NormalZ=1 AngleXU=0 Radius=5 StartAngle=1.11001e-11 EndAngle=1.5708
    g5: ArcOfCircle CenterX=-15 CenterY=5 CenterZ=0 NormalX=0 NormalY=0 NormalZ=1 AngleXU=0 Radius=5 StartAngle=1.5708 EndAngle=3.14159
  constraints (15):
    c: Coincident(g1,g2)
    c: Coincident(g2,g3)
    c: Vertical(g1)
    c: Vertical(g3)
    c: PointOnObject(g1,g-1)
    c: Tangent(g1,g4) = 1.5708
    c: Tangent(g0,g4) = 1.5708
    c: Tangent(g0,g5) = 1.5708
    c: Tangent(g3,g5) = 1.5708
    c: Horizontal(g0)
    c: DistanceX(g2,g2) = 40
    c: Symmetric(g2,g1,g-2)
    c: Distance(g-1,g0) = 10
    c: Radius(g5) = 5
    c: Radius(g4) = 5
FEATURE [PartDesign::Pocket] Pocket015
  BaseFeature = -> Pocket014
  Direction = (-1,0,0)
  Length = 5
  Length2 = 5
  Profile = -> Sketch018
  ReferenceAxis = -> Sketch018 [N_Axis]
  Type = 1
FEATURE [Sketcher::SketchObject] Sketch019
  FullyConstrained = true
  MapMode = 5
  Placement = pos=(0,-25,0) rot=(1,0,0;1.5708rad)
  Support = -> [Pocket014]
  sketch-geometry (6):
    g0: LineSegment StartX=-15 StartY=10 StartZ=0 EndX=15 EndY=10 EndZ=0
    g1: LineSegment StartX=20 StartY=5 StartZ=0 EndX=20 EndY=0 EndZ=0
    g2: LineSegment StartX=20 StartY=0 StartZ=0 EndX=-20 EndY=0 EndZ=0
    g3: LineSegment StartX=-20 StartY=0 StartZ=0 EndX=-20 EndY=5 EndZ=0
    g4: ArcOfCircle CenterX=15 CenterY=5 CenterZ=0 NormalX=0 NormalY=0 NormalZ=1 AngleXU=0 Radius=5 StartAngle=1.11e-11 EndAngle=1.5708
    g5: ArcOfCircle CenterX=-15 CenterY=5 CenterZ=0 NormalX=0 NormalY=0 NormalZ=1 AngleXU=0 Radius=5 StartAngle=1.5708 EndAngle=3.14159
  constraints (15):
    c: Coincident(g1,g2)
    c: Coincident(g2,g3)
    c: Horizontal(g0)
    c: Vertical(g1)
    c: Vertical(g3)
    c: Symmetric(g2,g1,g-2)
    c: PointOnObject(g1,g-1)
    c: Tangent(g0,g4) = 1.5708
    c: Tangent(g1,g4) = 1.5708
    c: Tangent(g0,g5) = 1.5708
    c: Tangent(g3,g5) = 1.5708
    c: DistanceX(g2,g2) = 40
    c: Distance(g-1,g0) = 10
    c: Radius(g5) = 5
    c: Radius(g4) = 5
FEATURE [PartDesign::Pocket] Pocket016
  BaseFeature = -> Pocket015
  Direction = (0,1,-2e-16)
  Length = 5
  Length2 = 5
  Profile = -> Sketch019
  ReferenceAxis = -> Sketch019 [N_Axis]
  Type = 1
FEATURE [Sketcher::SketchObject] Sketch020
  FullyConstrained = false
  MapMode = 5
  Placement = pos=(0,0,20) rot=(0,0,1;0rad)
  sketch-geometry (4):
    g0: Circle CenterX=-20 CenterY=20 CenterZ=0 NormalX=0 NormalY=0 NormalZ=1 AngleXU=0 Radius=1.55
    g1: Circle CenterX=20 CenterY=20 CenterZ=0 NormalX=0 NormalY=0 NormalZ=1 AngleXU=0 Radius=1.55
    g2: Circle CenterX=20 CenterY=-20 CenterZ=0 NormalX=0 NormalY=0 NormalZ=1 AngleXU=0 Radius=1.55
    g3: Circle CenterX=-20 CenterY=-20 CenterZ=0 NormalX=0 NormalY=0 NormalZ=1 AngleXU=0 Radius=1.55
  constraints (4):
    c: Diameter(g0) = 3.1
    c: Diameter(g1) = 3.1
    c: Diameter(g2) = 3.1
    c: Diameter(g3) = 3.1
FEATURE [PartDesign::Pocket] Pocket017
  BaseFeature = -> Pocket016
  Direction = (0,0,-1)
  Length = 5
  Length2 = 5
  Profile = -> Sketch020
  ReferenceAxis = -> Sketch020 [N_Axis]
  Type = 0
FEATURE [Sketcher::SketchObject] Sketch021
  ExternalGeometry = -> [Pocket017]
  FullyConstrained = true
  MapMode = 5
  Placement = pos=(0,-25,0) rot=(1,0,0;1.5708rad)
  Support = -> [Pocket017]
  sketch-geometry (2):
    g0: Circle CenterX=-20 CenterY=14 CenterZ=0 NormalX=0 NormalY=0 NormalZ=1 AngleXU=0 Radius=1.4
    g1: Circle CenterX=20 CenterY=14 CenterZ=0 NormalX=0 NormalY=0 NormalZ=1 AngleXU=0 Radius=1.4
  constraints (6):
    c: Diameter(g0) = 2.8
    c: Diameter(g1) = 2.8
    c: Distance(g0,g-5) = 5
    c: Distance(g0,g-3) = 6
    c: Distance(g1,g-3) = 6
    c: Distance(g1,g-4) = 5
FEATURE [PartDesign::Pocket] Pocket018
  BaseFeature = -> Pocket017
  Direction = (0,1,-2e-16)
  Length = 3
  Length2 = 5
  Profile = -> Sketch021
  ReferenceAxis = -> Sketch021 [N_Axis]
  Type = 0
FEATURE [PartDesign::Body] Body004  label="BackplaneBlock002"
  Group = -> [Sketch016,Pad003,Sketch017,Pocket014,Sketch018,Sketch019,Pocket015,Pocket016,Sketch020,Pocket017,Sketch021,Pocket018]
  Origin = -> Origin004
  Placement = pos=(85,145,0) rot=(0,0,1;3.14159rad)
  Tip = -> Pocket018
FEATURE [Sketcher::SketchObject] Sketch022
  FullyConstrained = true
  MapMode = 5
  Support = -> [XY_Plane005]
  sketch-geometry (4):
    g0: LineSegment StartX=-25 StartY=25 StartZ=0 EndX=25 EndY=25 EndZ=0
    g1: LineSegment StartX=25 StartY=25 StartZ=0 EndX=25 EndY=-25 EndZ=0
    g2: LineSegment StartX=25 StartY=-25 StartZ=0 EndX=-25 EndY=-25 EndZ=0
    g3: LineSegment StartX=-25 StartY=-25 StartZ=0 EndX=-25 EndY=25 EndZ=0
  constraints (10):
    c: Coincident(g0,g1)
    c: Coincident(g1,g2)
    c: Coincident(g2,g3)
    c: Coincident(g3,g0)
    c: Horizontal(g0)
    c: Vertical(g3)
    c: Symmetric(g2,g1,g-2)
    c: Symmetric(g1,g0,g-1)
    c: DistanceY(g1,g1) = 50
    c: DistanceX(g2,g2) = 50
FEATURE [PartDesign::Pad] Pad004
  Direction = (0,0,1)
  Length = 20
  Length2 = 10
  Profile = -> Sketch022
  ReferenceAxis = -> Sketch022 [N_Axis]
  Type = 0
FEATURE [Sketcher::SketchObject] Sketch023
  ExternalGeometry = -> [Pad004]
  FullyConstrained = true
  MapMode = 5
  Placement = pos=(0,0,20) rot=(0,0,1;0rad)
  Support = -> [Pad004]
  sketch-geometry (36):
    g0: LineSegment StartX=-18 StartY=15 StartZ=0 EndX=-17 EndY=15 EndZ=0
    g1: LineSegment StartX=20 StartY=13 StartZ=0 EndX=20 EndY=-13 EndZ=0
    g2: LineSegment StartX=18 StartY=-15 StartZ=0 EndX=17 EndY=-15 EndZ=0
    g3: LineSegment StartX=-20 StartY=-13 StartZ=0 EndX=-20 EndY=13 EndZ=0
    g4: LineSegment StartX=-13 StartY=20 StartZ=0 EndX=13 EndY=20 EndZ=0
    g5: LineSegment StartX=15 StartY=18 StartZ=0 EndX=15 EndY=17 EndZ=0
    g6: LineSegment StartX=13 StartY=-20 StartZ=0 EndX=-13 EndY=-20 EndZ=0
    g7: LineSegment StartX=-15 StartY=-18 StartZ=0 EndX=-15 EndY=-17 EndZ=0
    g8: LineSegment StartX=17 StartY=15 StartZ=0 EndX=18 EndY=15 EndZ=0
    g9: LineSegment StartX=-15 StartY=17 StartZ=0 EndX=-15 EndY=18 EndZ=0
    g10: LineSegment StartX=-17 StartY=-15 StartZ=0 EndX=-18 EndY=-15 EndZ=0
    g11: LineSegment StartX=15 StartY=-17 StartZ=0 EndX=15 EndY=-18 EndZ=0
    g12: ArcOfCircle CenterX=-13 CenterY=-18 CenterZ=0 NormalX=0 NormalY=0 NormalZ=1 AngleXU=0 Radius=2 StartAngle=3.14159 EndAngle=4.71239
    g13: GeomPoint X=-15 Y=-20 Z=0
    g14: ArcOfCircle CenterX=13 CenterY=-18 CenterZ=0 NormalX=0 NormalY=0 NormalZ=1 AngleXU=0 Radius=2 StartAngle=4.71239 EndAngle=6.28319
    g15: GeomPoint X=15 Y=-20 Z=0
    g16: ArcOfCircle CenterX=17 CenterY=-17 CenterZ=0 NormalX=0 NormalY=0 NormalZ=1 AngleXU=0 Radius=2 StartAngle=1.5708 EndAngle=3.14159
    g17: GeomPoint X=15 Y=-15 Z=0
    g18: ArcOfCircle CenterX=18 CenterY=-13 CenterZ=0 NormalX=0 NormalY=0 NormalZ=1 AngleXU=0 Radius=2 StartAngle=4.71239 EndAngle=6.28319
    g19: GeomPoint X=20 Y=-15 Z=0
    g20: ArcOfCircle CenterX=18 CenterY=13 CenterZ=0 NormalX=0 NormalY=0 NormalZ=1 AngleXU=0 Radius=2 StartAngle=0 EndAngle=1.5708
    g21: GeomPoint X=20 Y=15 Z=0
    g22: ArcOfCircle CenterX=17 CenterY=17 CenterZ=0 NormalX=0 NormalY=0 NormalZ=1 AngleXU=0 Radius=2 StartAngle=3.14159 EndAngle=4.71239
    g23: GeomPoint X=15 Y=15 Z=0
    g24: ArcOfCircle CenterX=13 CenterY=18 CenterZ=0 NormalX=0 NormalY=0 NormalZ=1 AngleXU=0 Radius=2 StartAngle=4e-16 EndAngle=1.5708
    g25: GeomPoint X=15 Y=20 Z=0
    g26: ArcOfCircle CenterX=-13 CenterY=18 CenterZ=0 NormalX=0 NormalY=0 NormalZ=1 AngleXU=0 Radius=2 StartAngle=1.5708 EndAngle=3.14159
    g27: GeomPoint X=-15 Y=20 Z=0
    g28: ArcOfCircle CenterX=-17 CenterY=17 CenterZ=0 NormalX=0 NormalY=0 NormalZ=1 AngleXU=0 Radius=2 StartAngle=4.71239 EndAngle=6.28319
    g29: GeomPoint X=-15 Y=15 Z=0
    g30: ArcOfCircle CenterX=-18 CenterY=13 CenterZ=0 NormalX=0 NormalY=0 NormalZ=1 AngleXU=0 Radius=2 StartAngle=1.5708 EndAngle=3.14159
    g31: GeomPoint X=-20 Y=15 Z=0
    g32: ArcOfCircle CenterX=-18 CenterY=-13 CenterZ=0 NormalX=0 NormalY=0 NormalZ=1 AngleXU=0 Radius=2 StartAngle=3.14159 EndAngle=4.71239
    g33: GeomPoint X=-20 Y=-15 Z=0
    g34: ArcOfCircle CenterX=-17 CenterY=-17 CenterZ=0 NormalX=0 NormalY=0 NormalZ=1 AngleXU=0 Radius=2 StartAngle=0 EndAngle=1.5708
    g35: GeomPoint X=-15 Y=-15 Z=0
  constraints (80):
    c: Horizontal(g2)
    c: Vertical(g3)
    c: Symmetric(g21,g31,g-2)
    c: Symmetric(g21,g19,g-1)
    c: DistanceX(g31,g21) = 40
    c: DistanceY(g19,g21) = 30
    c: Horizontal(g4)
    c: Vertical(g7)
    c: Symmetric(g13,g15,g-2)
    c: Symmetric(g15,g25,g-1)
    c: DistanceY(g15,g25) = 40
    c: Vertical(g9)
    c: Vertical(g5)
    c: Vertical(g11)
    c: Horizontal(g10)
    c: Horizontal(g8)
    c: Horizontal(g0)
    c: DistanceX(g13,g15) = 30
    c: DistanceY(g33,g31) = 30
    c: DistanceX(g27,g25) = 30
    c: PointOnObject(g13,g7)
    c: PointOnObject(g13,g6)
    c: Tangent(g7,g12) = 1.5708
    c: Tangent(g6,g12) = 1.5708
    c: Radius(g12) = 2
    c: PointOnObject(g15,g11)
    c: PointOnObject(g15,g6)
    c: Tangent(g11,g14) = 1.5708
    c: Tangent(g6,g14) = 1.5708
    c: PointOnObject(g17,g11)
    c: PointOnObject(g17,g2)
    c: Tangent(g11,g16) = -1.5708
    c: Tangent(g2,g16) = -1.5708
    c: PointOnObject(g19,g2)
    c: PointOnObject(g19,g1)
    c: Tangent(g2,g18) = 1.5708
    c: Tangent(g1,g18) = 1.5708
    c: PointOnObject(g21,g1)
    c: PointOnObject(g21,g8)
    c: Tangent(g1,g20) = 1.5708
    c: Tangent(g8,g20) = 1.5708
    c: PointOnObject(g23,g8)
    c: PointOnObject(g23,g5)
    c: Tangent(g8,g22) = -1.5708
    c: Tangent(g5,g22) = -1.5708
    c: PointOnObject(g25,g5)
    c: PointOnObject(g25,g4)
    c: Tangent(g5,g24) = 1.5708
    c: Tangent(g4,g24) = 1.5708
    c: PointOnObject(g27,g9)
    c: PointOnObject(g27,g4)
    c: Tangent(g9,g26) = 1.5708
    c: Tangent(g4,g26) = 1.5708
    c: PointOnObject(g29,g9)
    c: PointOnObject(g29,g0)
    c: Tangent(g9,g28) = -1.5708
    c: Tangent(g0,g28) = -1.5708
    c: PointOnObject(g31,g0)
    c: PointOnObject(g31,g3)
    c: Tangent(g0,g30) = 1.5708
    c: Tangent(g3,g30) = 1.5708
    c: PointOnObject(g33,g3)
    c: PointOnObject(g33,g10)
    c: Tangent(g3,g32) = 1.5708
    c: Tangent(g10,g32) = 1.5708
    c: PointOnObject(g35,g10)
    c: PointOnObject(g35,g7)
    c: Tangent(g10,g34) = -1.5708
    c: Tangent(g7,g34) = -1.5708
    c: Radius(g34) = 2
    c: Radius(g32) = 2
    c: Radius(g30) = 2
    c: Radius(g28) = 2
    c: Radius(g26) = 2
    c: Radius(g24) = 2
    c: Radius(g22) = 2
    c: Radius(g20) = 2
    c: Radius(g18) = 2
    c: Radius(g16) = 2
    c: Radius(g14) = 2
FEATURE [PartDesign::Pocket] Pocket019
  BaseFeature = -> Pad004
  Direction = (0,0,-1)
  Length = 5
  Length2 = 5
  Profile = -> Sketch023
  ReferenceAxis = -> Sketch023 [N_Axis]
  Type = 1
FEATURE [Sketcher::SketchObject] Sketch024
  ExternalGeometry = -> [Pocket019]
  FullyConstrained = true
  MapMode = 5
  Placement = pos=(25,0,0) rot=(0.57735,0.57735,0.57735;2.0944rad)
  Support = -> [Pocket019]
  sketch-geometry (6):
    g0: LineSegment StartX=-15 StartY=10 StartZ=0 EndX=15 EndY=10 EndZ=0
    g1: LineSegment StartX=20 StartY=5 StartZ=0 EndX=20 EndY=0 EndZ=0
    g2: LineSegment StartX=20 StartY=0 StartZ=0 EndX=-20 EndY=0 EndZ=0
    g3: LineSegment StartX=-20 StartY=0 StartZ=0 EndX=-20 EndY=5 EndZ=0
    g4: ArcOfCircle CenterX=15 CenterY=5 CenterZ=0 NormalX=0 NormalY=0 NormalZ=1 AngleXU=0 Radius=5 StartAngle=1.11001e-11 EndAngle=1.5708
    g5: ArcOfCircle CenterX=-15 CenterY=5 CenterZ=0 NormalX=0 NormalY=0 NormalZ=1 AngleXU=0 Radius=5 StartAngle=1.5708 EndAngle=3.14159
  constraints (15):
    c: Coincident(g1,g2)
    c: Coincident(g2,g3)
    c: Vertical(g1)
    c: Vertical(g3)
    c: PointOnObject(g1,g-1)
    c: Tangent(g1,g4) = 1.5708
    c: Tangent(g0,g4) = 1.5708
    c: Tangent(g0,g5) = 1.5708
    c: Tangent(g3,g5) = 1.5708
    c: Horizontal(g0)
    c: DistanceX(g2,g2) = 40
    c: Symmetric(g2,g1,g-2)
    c: Distance(g-1,g0) = 10
    c: Radius(g5) = 5
    c: Radius(g4) = 5
FEATURE [PartDesign::Pocket] Pocket020
  BaseFeature = -> Pocket019
  Direction = (-1,0,0)
  Length = 5
  Length2 = 5
  Profile = -> Sketch024
  ReferenceAxis = -> Sketch024 [N_Axis]
  Type = 1
FEATURE [Sketcher::SketchObject] Sketch025
  FullyConstrained = true
  MapMode = 5
  Placement = pos=(0,-25,0) rot=(1,0,0;1.5708rad)
  Support = -> [Pocket019]
  sketch-geometry (6):
    g0: LineSegment StartX=-15 StartY=10 StartZ=0 EndX=15 EndY=10 EndZ=0
    g1: LineSegment StartX=20 StartY=5 StartZ=0 EndX=20 EndY=0 EndZ=0
    g2: LineSegment StartX=20 StartY=0 StartZ=0 EndX=-20 EndY=0 EndZ=0
    g3: LineSegment StartX=-20 StartY=0 StartZ=0 EndX=-20 EndY=5 EndZ=0
    g4: ArcOfCircle CenterX=15 CenterY=5 CenterZ=0 NormalX=0 NormalY=0 NormalZ=1 AngleXU=0 Radius=5 StartAngle=1.11e-11 EndAngle=1.5708
    g5: ArcOfCircle CenterX=-15 CenterY=5 CenterZ=0 NormalX=0 NormalY=0 NormalZ=1 AngleXU=0 Radius=5 StartAngle=1.5708 EndAngle=3.14159
  constraints (15):
    c: Coincident(g1,g2)
    c: Coincident(g2,g3)
    c: Horizontal(g0)
    c: Vertical(g1)
    c: Vertical(g3)
    c: Symmetric(g2,g1,g-2)
    c: PointOnObject(g1,g-1)
    c: Tangent(g0,g4) = 1.5708
    c: Tangent(g1,g4) = 1.5708
    c: Tangent(g0,g5) = 1.5708
    c: Tangent(g3,g5) = 1.5708
    c: DistanceX(g2,g2) = 40
    c: Distance(g-1,g0) = 10
    c: Radius(g5) = 5
    c: Radius(g4) = 5
FEATURE [PartDesign::Pocket] Pocket021
  BaseFeature = -> Pocket020
  Direction = (0,1,-2e-16)
  Length = 5
  Length2 = 5
  Profile = -> Sketch025
  ReferenceAxis = -> Sketch025 [N_Axis]
  Type = 1
FEATURE [Sketcher::SketchObject] Sketch026
  FullyConstrained = false
  MapMode = 5
  Placement = pos=(0,0,20) rot=(0,0,1;0rad)
  sketch-geometry (4):
    g0: Circle CenterX=-20 CenterY=20 CenterZ=0 NormalX=0 NormalY=0 NormalZ=1 AngleXU=0 Radius=1.55
    g1: Circle CenterX=20 CenterY=20 CenterZ=0 NormalX=0 NormalY=0 NormalZ=1 AngleXU=0 Radius=1.55
    g2: Circle CenterX=20 CenterY=-20 CenterZ=0 NormalX=0 NormalY=0 NormalZ=1 AngleXU=0 Radius=1.55
    g3: Circle CenterX=-20 CenterY=-20 CenterZ=0 NormalX=0 NormalY=0 NormalZ=1 AngleXU=0 Radius=1.55
  constraints (4):
    c: Diameter(g0) = 3.1
    c: Diameter(g1) = 3.1
    c: Diameter(g2) = 3.1
    c: Diameter(g3) = 3.1
FEATURE [PartDesign::Pocket] Pocket022
  BaseFeature = -> Pocket021
  Direction = (0,0,-1)
  Length = 5
  Length2 = 5
  Profile = -> Sketch026
  ReferenceAxis = -> Sketch026 [N_Axis]
  Type = 0
FEATURE [Sketcher::SketchObject] Sketch027
  ExternalGeometry = -> [Pocket022]
  FullyConstrained = true
  MapMode = 5
  Placement = pos=(0,-25,0) rot=(1,0,0;1.5708rad)
  Support = -> [Pocket022]
  sketch-geometry (2):
    g0: Circle CenterX=-20 CenterY=14 CenterZ=0 NormalX=0 NormalY=0 NormalZ=1 AngleXU=0 Radius=1.4
    g1: Circle CenterX=20 CenterY=14 CenterZ=0 NormalX=0 NormalY=0 NormalZ=1 AngleXU=0 Radius=1.4
  constraints (6):
    c: Diameter(g0) = 2.8
    c: Diameter(g1) = 2.8
    c: Distance(g0,g-5) = 5
    c: Distance(g0,g-3) = 6
    c: Distance(g1,g-3) = 6
    c: Distance(g1,g-4) = 5
FEATURE [PartDesign::Pocket] Pocket023
  BaseFeature = -> Pocket022
  Direction = (0,1,-2e-16)
  Length = 3
  Length2 = 5
  Profile = -> Sketch027
  ReferenceAxis = -> Sketch027 [N_Axis]
  Type = 0
FEATURE [PartDesign::Body] Body005  label="BackplaneBlock003"
  Group = -> [Sketch022,Pad004,Sketch023,Pocket019,Sketch024,Sketch025,Pocket020,Pocket021,Sketch026,Pocket022,Sketch027,Pocket023]
  Origin = -> Origin005
  Placement = pos=(25,85,0) rot=(0,0,-1;1.5708rad)
  Tip = -> Pocket023
FEATURE [Sketcher::SketchObject] Sketch028
  FullyConstrained = true
  MapMode = 5
  Support = -> [XY_Plane006]
  sketch-geometry (4):
    g0: LineSegment StartX=-25 StartY=25 StartZ=0 EndX=25 EndY=25 EndZ=0
    g1: LineSegment StartX=25 StartY=25 StartZ=0 EndX=25 EndY=-25 EndZ=0
    g2: LineSegment StartX=25 StartY=-25 StartZ=0 EndX=-25 EndY=-25 EndZ=0
    g3: LineSegment StartX=-25 StartY=-25 StartZ=0 EndX=-25 EndY=25 EndZ=0
  constraints (10):
    c: Coincident(g0,g1)
    c: Coincident(g1,g2)
    c: Coincident(g2,g3)
    c: Coincident(g3,g0)
    c: Horizontal(g0)
    c: Vertical(g3)
    c: Symmetric(g2,g1,g-2)
    c: Symmetric(g1,g0,g-1)
    c: DistanceY(g1,g1) = 50
    c: DistanceX(g2,g2) = 50
FEATURE [PartDesign::Pad] Pad005
  Direction = (0,0,1)
  Length = 20
  Length2 = 10
  Profile = -> Sketch028
  ReferenceAxis = -> Sketch028 [N_Axis]
  Type = 0
FEATURE [Sketcher::SketchObject] Sketch029
  ExternalGeometry = -> [Pad005]
  FullyConstrained = true
  MapMode = 5
  Placement = pos=(0,0,20) rot=(0,0,1;0rad)
  Support = -> [Pad005]
  sketch-geometry (36):
    g0: LineSegment StartX=-18 StartY=15 StartZ=0 EndX=-17 EndY=15 EndZ=0
    g1: LineSegment StartX=20 StartY=13 StartZ=0 EndX=20 EndY=-13 EndZ=0
    g2: LineSegment StartX=18 StartY=-15 StartZ=0 EndX=17 EndY=-15 EndZ=0
    g3: LineSegment StartX=-20 StartY=-13 StartZ=0 EndX=-20 EndY=13 EndZ=0
    g4: LineSegment StartX=-13 StartY=20 StartZ=0 EndX=13 EndY=20 EndZ=0
    g5: LineSegment StartX=15 StartY=18 StartZ=0 EndX=15 EndY=17 EndZ=0
    g6: LineSegment StartX=13 StartY=-20 StartZ=0 EndX=-13 EndY=-20 EndZ=0
    g7: LineSegment StartX=-15 StartY=-18 StartZ=0 EndX=-15 EndY=-17 EndZ=0
    g8: LineSegment StartX=17 StartY=15 StartZ=0 EndX=18 EndY=15 EndZ=0
    g9: LineSegment StartX=-15 StartY=17 StartZ=0 EndX=-15 EndY=18 EndZ=0
    g10: LineSegment StartX=-17 StartY=-15 StartZ=0 EndX=-18 EndY=-15 EndZ=0
    g11: LineSegment StartX=15 StartY=-17 StartZ=0 EndX=15 EndY=-18 EndZ=0
    g12: ArcOfCircle CenterX=-13 CenterY=-18 CenterZ=0 NormalX=0 NormalY=0 NormalZ=1 AngleXU=0 Radius=2 StartAngle=3.14159 EndAngle=4.71239
    g13: GeomPoint X=-15 Y=-20 Z=0
    g14: ArcOfCircle CenterX=13 CenterY=-18 CenterZ=0 NormalX=0 NormalY=0 NormalZ=1 AngleXU=0 Radius=2 StartAngle=4.71239 EndAngle=6.28319
    g15: GeomPoint X=15 Y=-20 Z=0
    g16: ArcOfCircle CenterX=17 CenterY=-17 CenterZ=0 NormalX=0 NormalY=0 NormalZ=1 AngleXU=0 Radius=2 StartAngle=1.5708 EndAngle=3.14159
    g17: GeomPoint X=15 Y=-15 Z=0
    g18: ArcOfCircle CenterX=18 CenterY=-13 CenterZ=0 NormalX=0 NormalY=0 NormalZ=1 AngleXU=0 Radius=2 StartAngle=4.71239 EndAngle=6.28319
    g19: GeomPoint X=20 Y=-15 Z=0
    g20: ArcOfCircle CenterX=18 CenterY=13 CenterZ=0 NormalX=0 NormalY=0 NormalZ=1 AngleXU=0 Radius=2 StartAngle=0 EndAngle=1.5708
    g21: GeomPoint X=20 Y=15 Z=0
    g22: ArcOfCircle CenterX=17 CenterY=17 CenterZ=0 NormalX=0 NormalY=0 NormalZ=1 AngleXU=0 Radius=2 StartAngle=3.14159 EndAngle=4.71239
    g23: GeomPoint X=15 Y=15 Z=0
    g24: ArcOfCircle CenterX=13 CenterY=18 CenterZ=0 NormalX=0 NormalY=0 NormalZ=1 AngleXU=0 Radius=2 StartAngle=4e-16 EndAngle=1.5708
    g25: GeomPoint X=15 Y=20 Z=0
    g26: ArcOfCircle CenterX=-13 CenterY=18 CenterZ=0 NormalX=0 NormalY=0 NormalZ=1 AngleXU=0 Radius=2 StartAngle=1.5708 EndAngle=3.14159
    g27: GeomPoint X=-15 Y=20 Z=0
    g28: ArcOfCircle CenterX=-17 CenterY=17 CenterZ=0 NormalX=0 NormalY=0 NormalZ=1 AngleXU=0 Radius=2 StartAngle=4.71239 EndAngle=6.28319
    g29: GeomPoint X=-15 Y=15 Z=0
    g30: ArcOfCircle CenterX=-18 CenterY=13 CenterZ=0 NormalX=0 NormalY=0 NormalZ=1 AngleXU=0 Radius=2 StartAngle=1.5708 EndAngle=3.14159
    g31: GeomPoint X=-20 Y=15 Z=0
    g32: ArcOfCircle CenterX=-18 CenterY=-13 CenterZ=0 NormalX=0 NormalY=0 NormalZ=1 AngleXU=0 Radius=2 StartAngle=3.14159 EndAngle=4.71239
    g33: GeomPoint X=-20 Y=-15 Z=0
    g34: ArcOfCircle CenterX=-17 CenterY=-17 CenterZ=0 NormalX=0 NormalY=0 NormalZ=1 AngleXU=0 Radius=2 StartAngle=0 EndAngle=1.5708
    g35: GeomPoint X=-15 Y=-15 Z=0
  constraints (80):
    c: Horizontal(g2)
    c: Vertical(g3)
    c: Symmetric(g21,g31,g-2)
    c: Symmetric(g21,g19,g-1)
    c: DistanceX(g31,g21) = 40
    c: DistanceY(g19,g21) = 30
    c: Horizontal(g4)
    c: Vertical(g7)
    c: Symmetric(g13,g15,g-2)
    c: Symmetric(g15,g25,g-1)
    c: DistanceY(g15,g25) = 40
    c: Vertical(g9)
    c: Vertical(g5)
    c: Vertical(g11)
    c: Horizontal(g10)
    c: Horizontal(g8)
    c: Horizontal(g0)
    c: DistanceX(g13,g15) = 30
    c: DistanceY(g33,g31) = 30
    c: DistanceX(g27,g25) = 30
    c: PointOnObject(g13,g7)
    c: PointOnObject(g13,g6)
    c: Tangent(g7,g12) = 1.5708
    c: Tangent(g6,g12) = 1.5708
    c: Radius(g12) = 2
    c: PointOnObject(g15,g11)
    c: PointOnObject(g15,g6)
    c: Tangent(g11,g14) = 1.5708
    c: Tangent(g6,g14) = 1.5708
    c: PointOnObject(g17,g11)
    c: PointOnObject(g17,g2)
    c: Tangent(g11,g16) = -1.5708
    c: Tangent(g2,g16) = -1.5708
    c: PointOnObject(g19,g2)
    c: PointOnObject(g19,g1)
    c: Tangent(g2,g18) = 1.5708
    c: Tangent(g1,g18) = 1.5708
    c: PointOnObject(g21,g1)
    c: PointOnObject(g21,g8)
    c: Tangent(g1,g20) = 1.5708
    c: Tangent(g8,g20) = 1.5708
    c: PointOnObject(g23,g8)
    c: PointOnObject(g23,g5)
    c: Tangent(g8,g22) = -1.5708
    c: Tangent(g5,g22) = -1.5708
    c: PointOnObject(g25,g5)
    c: PointOnObject(g25,g4)
    c: Tangent(g5,g24) = 1.5708
    c: Tangent(g4,g24) = 1.5708
    c: PointOnObject(g27,g9)
    c: PointOnObject(g27,g4)
    c: Tangent(g9,g26) = 1.5708
    c: Tangent(g4,g26) = 1.5708
    c: PointOnObject(g29,g9)
    c: PointOnObject(g29,g0)
    c: Tangent(g9,g28) = -1.5708
    c: Tangent(g0,g28) = -1.5708
    c: PointOnObject(g31,g0)
    c: PointOnObject(g31,g3)
    c: Tangent(g0,g30) = 1.5708
    c: Tangent(g3,g30) = 1.5708
    c: PointOnObject(g33,g3)
    c: PointOnObject(g33,g10)
    c: Tangent(g3,g32) = 1.5708
    c: Tangent(g10,g32) = 1.5708
    c: PointOnObject(g35,g10)
    c: PointOnObject(g35,g7)
    c: Tangent(g10,g34) = -1.5708
    c: Tangent(g7,g34) = -1.5708
    c: Radius(g34) = 2
    c: Radius(g32) = 2
    c: Radius(g30) = 2
    c: Radius(g28) = 2
    c: Radius(g26) = 2
    c: Radius(g24) = 2
    c: Radius(g22) = 2
    c: Radius(g20) = 2
    c: Radius(g18) = 2
    c: Radius(g16) = 2
    c: Radius(g14) = 2
FEATURE [PartDesign::Pocket] Pocket024
  BaseFeature = -> Pad005
  Direction = (0,0,-1)
  Length = 5
  Length2 = 5
  Profile = -> Sketch029
  ReferenceAxis = -> Sketch029 [N_Axis]
  Type = 1
FEATURE [Sketcher::SketchObject] Sketch030
  ExternalGeometry = -> [Pocket024]
  FullyConstrained = true
  MapMode = 5
  Placement = pos=(25,0,0) rot=(0.57735,0.57735,0.57735;2.0944rad)
  Support = -> [Pocket024]
  sketch-geometry (6):
    g0: LineSegment StartX=-15 StartY=10 StartZ=0 EndX=15 EndY=10 EndZ=0
    g1: LineSegment StartX=20 StartY=5 StartZ=0 EndX=20 EndY=0 EndZ=0
    g2: LineSegment StartX=20 StartY=0 StartZ=0 EndX=-20 EndY=0 EndZ=0
    g3: LineSegment StartX=-20 StartY=0 StartZ=0 EndX=-20 EndY=5 EndZ=0
    g4: ArcOfCircle CenterX=15 CenterY=5 CenterZ=0 NormalX=0 NormalY=0 NormalZ=1 AngleXU=0 Radius=5 StartAngle=1.11001e-11 EndAngle=1.5708
    g5: ArcOfCircle CenterX=-15 CenterY=5 CenterZ=0 NormalX=0 NormalY=0 NormalZ=1 AngleXU=0 Radius=5 StartAngle=1.5708 EndAngle=3.14159
  constraints (15):
    c: Coincident(g1,g2)
    c: Coincident(g2,g3)
    c: Vertical(g1)
    c: Vertical(g3)
    c: PointOnObject(g1,g-1)
    c: Tangent(g1,g4) = 1.5708
    c: Tangent(g0,g4) = 1.5708
    c: Tangent(g0,g5) = 1.5708
    c: Tangent(g3,g5) = 1.5708
    c: Horizontal(g0)
    c: DistanceX(g2,g2) = 40
    c: Symmetric(g2,g1,g-2)
    c: Distance(g-1,g0) = 10
    c: Radius(g5) = 5
    c: Radius(g4) = 5
FEATURE [PartDesign::Pocket] Pocket025
  BaseFeature = -> Pocket024
  Direction = (-1,0,0)
  Length = 5
  Length2 = 5
  Profile = -> Sketch030
  ReferenceAxis = -> Sketch030 [N_Axis]
  Type = 1
FEATURE [Sketcher::SketchObject] Sketch031
  FullyConstrained = true
  MapMode = 5
  Placement = pos=(0,-25,0) rot=(1,0,0;1.5708rad)
  Support = -> [Pocket024]
  sketch-geometry (6):
    g0: LineSegment StartX=-15 StartY=10 StartZ=0 EndX=15 EndY=10 EndZ=0
    g1: LineSegment StartX=20 StartY=5 StartZ=0 EndX=20 EndY=0 EndZ=0
    g2: LineSegment StartX=20 StartY=0 StartZ=0 EndX=-20 EndY=0 EndZ=0
    g3: LineSegment StartX=-20 StartY=0 StartZ=0 EndX=-20 EndY=5 EndZ=0
    g4: ArcOfCircle CenterX=15 CenterY=5 CenterZ=0 NormalX=0 NormalY=0 NormalZ=1 AngleXU=0 Radius=5 StartAngle=1.11e-11 EndAngle=1.5708
    g5: ArcOfCircle CenterX=-15 CenterY=5 CenterZ=0 NormalX=0 NormalY=0 NormalZ=1 AngleXU=0 Radius=5 StartAngle=1.5708 EndAngle=3.14159
  constraints (15):
    c: Coincident(g1,g2)
    c: Coincident(g2,g3)
    c: Horizontal(g0)
    c: Vertical(g1)
    c: Vertical(g3)
    c: Symmetric(g2,g1,g-2)
    c: PointOnObject(g1,g-1)
    c: Tangent(g0,g4) = 1.5708
    c: Tangent(g1,g4) = 1.5708
    c: Tangent(g0,g5) = 1.5708
    c: Tangent(g3,g5) = 1.5708
    c: DistanceX(g2,g2) = 40
    c: Distance(g-1,g0) = 10
    c: Radius(g5) = 5
    c: Radius(g4) = 5
FEATURE [PartDesign::Pocket] Pocket026
  BaseFeature = -> Pocket025
  Direction = (0,1,-2e-16)
  Length = 5
  Length2 = 5
  Profile = -> Sketch031
  ReferenceAxis = -> Sketch031 [N_Axis]
  Type = 1
FEATURE [Sketcher::SketchObject] Sketch032
  FullyConstrained = false
  MapMode = 5
  Placement = pos=(0,0,20) rot=(0,0,1;0rad)
  sketch-geometry (4):
    g0: Circle CenterX=-20 CenterY=20 CenterZ=0 NormalX=0 NormalY=0 NormalZ=1 AngleXU=0 Radius=1.55
    g1: Circle CenterX=20 CenterY=20 CenterZ=0 NormalX=0 NormalY=0 NormalZ=1 AngleXU=0 Radius=1.55
    g2: Circle CenterX=20 CenterY=-20 CenterZ=0 NormalX=0 NormalY=0 NormalZ=1 AngleXU=0 Radius=1.55
    g3: Circle CenterX=-20 CenterY=-20 CenterZ=0 NormalX=0 NormalY=0 NormalZ=1 AngleXU=0 Radius=1.55
  constraints (4):
    c: Diameter(g0) = 3.1
    c: Diameter(g1) = 3.1
    c: Diameter(g2) = 3.1
    c: Diameter(g3) = 3.1
FEATURE [PartDesign::Pocket] Pocket027
  BaseFeature = -> Pocket026
  Direction = (0,0,-1)
  Length = 5
  Length2 = 5
  Profile = -> Sketch032
  ReferenceAxis = -> Sketch032 [N_Axis]
  Type = 0
FEATURE [Sketcher::SketchObject] Sketch033
  ExternalGeometry = -> [Pocket027]
  FullyConstrained = true
  MapMode = 5
  Placement = pos=(0,-25,0) rot=(1,0,0;1.5708rad)
  Support = -> [Pocket027]
  sketch-geometry (2):
    g0: Circle CenterX=-20 CenterY=14 CenterZ=0 NormalX=0 NormalY=0 NormalZ=1 AngleXU=0 Radius=1.4
    g1: Circle CenterX=20 CenterY=14 CenterZ=0 NormalX=0 NormalY=0 NormalZ=1 AngleXU=0 Radius=1.4
  constraints (6):
    c: Diameter(g0) = 2.8
    c: Diameter(g1) = 2.8
    c: Distance(g0,g-5) = 5
    c: Distance(g0,g-3) = 6
    c: Distance(g1,g-3) = 6
    c: Distance(g1,g-4) = 5
FEATURE [PartDesign::Pocket] Pocket028
  BaseFeature = -> Pocket027
  Direction = (0,1,-2e-16)
  Length = 3
  Length2 = 5
  Profile = -> Sketch033
  ReferenceAxis = -> Sketch033 [N_Axis]
  Type = 0
FEATURE [PartDesign::Body] Body006  label="BackplaneBlock004"
  Group = -> [Sketch028,Pad005,Sketch029,Pocket024,Sketch030,Sketch031,Pocket025,Pocket026,Sketch032,Pocket027,Sketch033,Pocket028]
  Origin = -> Origin006
  Placement = pos=(145,85,0) rot=(0,0,1;1.5708rad)
  Tip = -> Pocket028
FEATURE [Sketcher::SketchObject] Sketch034
  FullyConstrained = true
  MapMode = 5
  Support = -> [XY_Plane007]
  sketch-geometry (4):
    g0: LineSegment StartX=-25 StartY=25 StartZ=0 EndX=25 EndY=25 EndZ=0
    g1: LineSegment StartX=25 StartY=25 StartZ=0 EndX=25 EndY=-25 EndZ=0
    g2: LineSegment StartX=25 StartY=-25 StartZ=0 EndX=-25 EndY=-25 EndZ=0
    g3: LineSegment StartX=-25 StartY=-25 StartZ=0 EndX=-25 EndY=25 EndZ=0
  constraints (10):
    c: Coincident(g0,g1)
    c: Coincident(g1,g2)
    c: Coincident(g2,g3)
    c: Coincident(g3,g0)
    c: Horizontal(g0)
    c: Vertical(g3)
    c: Symmetric(g2,g1,g-2)
    c: Symmetric(g1,g0,g-1)
    c: DistanceY(g1,g1) = 50
    c: DistanceX(g2,g2) = 50
FEATURE [PartDesign::Pad] Pad006
  Direction = (0,0,1)
  Length = 20
  Length2 = 10
  Profile = -> Sketch034
  ReferenceAxis = -> Sketch034 [N_Axis]
  Type = 0
FEATURE [Sketcher::SketchObject] Sketch035
  ExternalGeometry = -> [Pad006]
  FullyConstrained = true
  MapMode = 5
  Placement = pos=(0,0,20) rot=(0,0,1;0rad)
  Support = -> [Pad006]
  sketch-geometry (36):
    g0: LineSegment StartX=-18 StartY=15 StartZ=0 EndX=-17 EndY=15 EndZ=0
    g1: LineSegment StartX=20 StartY=13 StartZ=0 EndX=20 EndY=-13 EndZ=0
    g2: LineSegment StartX=18 StartY=-15 StartZ=0 EndX=17 EndY=-15 EndZ=0
    g3: LineSegment StartX=-20 StartY=-13 StartZ=0 EndX=-20 EndY=13 EndZ=0
    g4: LineSegment StartX=-13 StartY=20 StartZ=0 EndX=13 EndY=20 EndZ=0
    g5: LineSegment StartX=15 StartY=18 StartZ=0 EndX=15 EndY=17 EndZ=0
    g6: LineSegment StartX=13 StartY=-20 StartZ=0 EndX=-13 EndY=-20 EndZ=0
    g7: LineSegment StartX=-15 StartY=-18 StartZ=0 EndX=-15 EndY=-17 EndZ=0
    g8: LineSegment StartX=17 StartY=15 StartZ=0 EndX=18 EndY=15 EndZ=0
    g9: LineSegment StartX=-15 StartY=17 StartZ=0 EndX=-15 EndY=18 EndZ=0
    g10: LineSegment StartX=-17 StartY=-15 StartZ=0 EndX=-18 EndY=-15 EndZ=0
    g11: LineSegment StartX=15 StartY=-17 StartZ=0 EndX=15 EndY=-18 EndZ=0
    g12: ArcOfCircle CenterX=-13 CenterY=-18 CenterZ=0 NormalX=0 NormalY=0 NormalZ=1 AngleXU=0 Radius=2 StartAngle=3.14159 EndAngle=4.71239
    g13: GeomPoint X=-15 Y=-20 Z=0
    g14: ArcOfCircle CenterX=13 CenterY=-18 CenterZ=0 NormalX=0 NormalY=0 NormalZ=1 AngleXU=0 Radius=2 StartAngle=4.71239 EndAngle=6.28319
    g15: GeomPoint X=15 Y=-20 Z=0
    g16: ArcOfCircle CenterX=17 CenterY=-17 CenterZ=0 NormalX=0 NormalY=0 NormalZ=1 AngleXU=0 Radius=2 StartAngle=1.5708 EndAngle=3.14159
    g17: GeomPoint X=15 Y=-15 Z=0
    g18: ArcOfCircle CenterX=18 CenterY=-13 CenterZ=0 NormalX=0 NormalY=0 NormalZ=1 AngleXU=0 Radius=2 StartAngle=4.71239 EndAngle=6.28319
    g19: GeomPoint X=20 Y=-15 Z=0
    g20: ArcOfCircle CenterX=18 CenterY=13 CenterZ=0 NormalX=0 NormalY=0 NormalZ=1 AngleXU=0 Radius=2 StartAngle=0 EndAngle=1.5708
    g21: GeomPoint X=20 Y=15 Z=0
    g22: ArcOfCircle CenterX=17 CenterY=17 CenterZ=0 NormalX=0 NormalY=0 NormalZ=1 AngleXU=0 Radius=2 StartAngle=3.14159 EndAngle=4.71239
    g23: GeomPoint X=15 Y=15 Z=0
    g24: ArcOfCircle CenterX=13 CenterY=18 CenterZ=0 NormalX=0 NormalY=0 NormalZ=1 AngleXU=0 Radius=2 StartAngle=4e-16 EndAngle=1.5708
    g25: GeomPoint X=15 Y=20 Z=0
    g26: ArcOfCircle CenterX=-13 CenterY=18 CenterZ=0 NormalX=0 NormalY=0 NormalZ=1 AngleXU=0 Radius=2 StartAngle=1.5708 EndAngle=3.14159
    g27: GeomPoint X=-15 Y=20 Z=0
    g28: ArcOfCircle CenterX=-17 CenterY=17 CenterZ=0 NormalX=0 NormalY=0 NormalZ=1 AngleXU=0 Radius=2 StartAngle=4.71239 EndAngle=6.28319
    g29: GeomPoint X=-15 Y=15 Z=0
    g30: ArcOfCircle CenterX=-18 CenterY=13 CenterZ=0 NormalX=0 NormalY=0 NormalZ=1 AngleXU=0 Radius=2 StartAngle=1.5708 EndAngle=3.14159
    g31: GeomPoint X=-20 Y=15 Z=0
    g32: ArcOfCircle CenterX=-18 CenterY=-13 CenterZ=0 NormalX=0 NormalY=0 NormalZ=1 AngleXU=0 Radius=2 StartAngle=3.14159 EndAngle=4.71239
    g33: GeomPoint X=-20 Y=-15 Z=0
    g34: ArcOfCircle CenterX=-17 CenterY=-17 CenterZ=0 NormalX=0 NormalY=0 NormalZ=1 AngleXU=0 Radius=2 StartAngle=0 EndAngle=1.5708
    g35: GeomPoint X=-15 Y=-15 Z=0
  constraints (80):
    c: Horizontal(g2)
    c: Vertical(g3)
    c: Symmetric(g21,g31,g-2)
    c: Symmetric(g21,g19,g-1)
    c: DistanceX(g31,g21) = 40
    c: DistanceY(g19,g21) = 30
    c: Horizontal(g4)
    c: Vertical(g7)
    c: Symmetric(g13,g15,g-2)
    c: Symmetric(g15,g25,g-1)
    c: DistanceY(g15,g25) = 40
    c: Vertical(g9)
    c: Vertical(g5)
    c: Vertical(g11)
    c: Horizontal(g10)
    c: Horizontal(g8)
    c: Horizontal(g0)
    c: DistanceX(g13,g15) = 30
    c: DistanceY(g33,g31) = 30
    c: DistanceX(g27,g25) = 30
    c: PointOnObject(g13,g7)
    c: PointOnObject(g13,g6)
    c: Tangent(g7,g12) = 1.5708
    c: Tangent(g6,g12) = 1.5708
    c: Radius(g12) = 2
    c: PointOnObject(g15,g11)
    c: PointOnObject(g15,g6)
    c: Tangent(g11,g14) = 1.5708
    c: Tangent(g6,g14) = 1.5708
    c: PointOnObject(g17,g11)
    c: PointOnObject(g17,g2)
    c: Tangent(g11,g16) = -1.5708
    c: Tangent(g2,g16) = -1.5708
    c: PointOnObject(g19,g2)
    c: PointOnObject(g19,g1)
    c: Tangent(g2,g18) = 1.5708
    c: Tangent(g1,g18) = 1.5708
    c: PointOnObject(g21,g1)
    c: PointOnObject(g21,g8)
    c: Tangent(g1,g20) = 1.5708
    c: Tangent(g8,g20) = 1.5708
    c: PointOnObject(g23,g8)
    c: PointOnObject(g23,g5)
    c: Tangent(g8,g22) = -1.5708
    c: Tangent(g5,g22) = -1.5708
    c: PointOnObject(g25,g5)
    c: PointOnObject(g25,g4)
    c: Tangent(g5,g24) = 1.5708
    c: Tangent(g4,g24) = 1.5708
    c: PointOnObject(g27,g9)
    c: PointOnObject(g27,g4)
    c: Tangent(g9,g26) = 1.5708
    c: Tangent(g4,g26) = 1.5708
    c: PointOnObject(g29,g9)
    c: PointOnObject(g29,g0)
    c: Tangent(g9,g28) = -1.5708
    c: Tangent(g0,g28) = -1.5708
    c: PointOnObject(g31,g0)
    c: PointOnObject(g31,g3)
    c: Tangent(g0,g30) = 1.5708
    c: Tangent(g3,g30) = 1.5708
    c: PointOnObject(g33,g3)
    c: PointOnObject(g33,g10)
    c: Tangent(g3,g32) = 1.5708
    c: Tangent(g10,g32) = 1.5708
    c: PointOnObject(g35,g10)
    c: PointOnObject(g35,g7)
    c: Tangent(g10,g34) = -1.5708
    c: Tangent(g7,g34) = -1.5708
    c: Radius(g34) = 2
    c: Radius(g32) = 2
    c: Radius(g30) = 2
    c: Radius(g28) = 2
    c: Radius(g26) = 2
    c: Radius(g24) = 2
    c: Radius(g22) = 2
    c: Radius(g20) = 2
    c: Radius(g18) = 2
    c: Radius(g16) = 2
    c: Radius(g14) = 2
FEATURE [PartDesign::Pocket] Pocket029
  BaseFeature = -> Pad006
  Direction = (0,0,-1)
  Length = 5
  Length2 = 5
  Profile = -> Sketch035
  ReferenceAxis = -> Sketch035 [N_Axis]
  Type = 1
FEATURE [Sketcher::SketchObject] Sketch036
  ExternalGeometry = -> [Pocket029]
  FullyConstrained = true
  MapMode = 5
  Placement = pos=(25,0,0) rot=(0.57735,0.57735,0.57735;2.0944rad)
  Support = -> [Pocket029]
  sketch-geometry (6):
    g0: LineSegment StartX=-15 StartY=10 StartZ=0 EndX=15 EndY=10 EndZ=0
    g1: LineSegment StartX=20 StartY=5 StartZ=0 EndX=20 EndY=0 EndZ=0
    g2: LineSegment StartX=20 StartY=0 StartZ=0 EndX=-20 EndY=0 EndZ=0
    g3: LineSegment StartX=-20 StartY=0 StartZ=0 EndX=-20 EndY=5 EndZ=0
    g4: ArcOfCircle CenterX=15 CenterY=5 CenterZ=0 NormalX=0 NormalY=0 NormalZ=1 AngleXU=0 Radius=5 StartAngle=1.11001e-11 EndAngle=1.5708
    g5: ArcOfCircle CenterX=-15 CenterY=5 CenterZ=0 NormalX=0 NormalY=0 NormalZ=1 AngleXU=0 Radius=5 StartAngle=1.5708 EndAngle=3.14159
  constraints (15):
    c: Coincident(g1,g2)
    c: Coincident(g2,g3)
    c: Vertical(g1)
    c: Vertical(g3)
    c: PointOnObject(g1,g-1)
    c: Tangent(g1,g4) = 1.5708
    c: Tangent(g0,g4) = 1.5708
    c: Tangent(g0,g5) = 1.5708
    c: Tangent(g3,g5) = 1.5708
    c: Horizontal(g0)
    c: DistanceX(g2,g2) = 40
    c: Symmetric(g2,g1,g-2)
    c: Distance(g-1,g0) = 10
    c: Radius(g5) = 5
    c: Radius(g4) = 5
FEATURE [PartDesign::Pocket] Pocket030
  BaseFeature = -> Pocket029
  Direction = (-1,0,0)
  Length = 5
  Length2 = 5
  Profile = -> Sketch036
  ReferenceAxis = -> Sketch036 [N_Axis]
  Type = 1
FEATURE [Sketcher::SketchObject] Sketch037
  FullyConstrained = true
  MapMode = 5
  Placement = pos=(0,-25,0) rot=(1,0,0;1.5708rad)
  Support = -> [Pocket029]
  sketch-geometry (6):
    g0: LineSegment StartX=-15 StartY=10 StartZ=0 EndX=15 EndY=10 EndZ=0
    g1: LineSegment StartX=20 StartY=5 StartZ=0 EndX=20 EndY=0 EndZ=0
    g2: LineSegment StartX=20 StartY=0 StartZ=0 EndX=-20 EndY=0 EndZ=0
    g3: LineSegment StartX=-20 StartY=0 StartZ=0 EndX=-20 EndY=5 EndZ=0
    g4: ArcOfCircle CenterX=15 CenterY=5 CenterZ=0 NormalX=0 NormalY=0 NormalZ=1 AngleXU=0 Radius=5 StartAngle=1.11e-11 EndAngle=1.5708
    g5: ArcOfCircle CenterX=-15 CenterY=5 CenterZ=0 NormalX=0 NormalY=0 NormalZ=1 AngleXU=0 Radius=5 StartAngle=1.5708 EndAngle=3.14159
  constraints (15):
    c: Coincident(g1,g2)
    c: Coincident(g2,g3)
    c: Horizontal(g0)
    c: Vertical(g1)
    c: Vertical(g3)
    c: Symmetric(g2,g1,g-2)
    c: PointOnObject(g1,g-1)
    c: Tangent(g0,g4) = 1.5708
    c: Tangent(g1,g4) = 1.5708
    c: Tangent(g0,g5) = 1.5708
    c: Tangent(g3,g5) = 1.5708
    c: DistanceX(g2,g2) = 40
    c: Distance(g-1,g0) = 10
    c: Radius(g5) = 5
    c: Radius(g4) = 5
FEATURE [PartDesign::Pocket] Pocket031
  BaseFeature = -> Pocket030
  Direction = (0,1,-2e-16)
  Length = 5
  Length2 = 5
  Profile = -> Sketch037
  ReferenceAxis = -> Sketch037 [N_Axis]
  Type = 1
FEATURE [Sketcher::SketchObject] Sketch038
  FullyConstrained = false
  MapMode = 5
  Placement = pos=(0,0,20) rot=(0,0,1;0rad)
  sketch-geometry (4):
    g0: Circle CenterX=-20 CenterY=20 CenterZ=0 NormalX=0 NormalY=0 NormalZ=1 AngleXU=0 Radius=1.55
    g1: Circle CenterX=20 CenterY=20 CenterZ=0 NormalX=0 NormalY=0 NormalZ=1 AngleXU=0 Radius=1.55
    g2: Circle CenterX=20 CenterY=-20 CenterZ=0 NormalX=0 NormalY=0 NormalZ=1 AngleXU=0 Radius=1.55
    g3: Circle CenterX=-20 CenterY=-20 CenterZ=0 NormalX=0 NormalY=0 NormalZ=1 AngleXU=0 Radius=1.55
  constraints (4):
    c: Diameter(g0) = 3.1
    c: Diameter(g1) = 3.1
    c: Diameter(g2) = 3.1
    c: Diameter(g3) = 3.1
FEATURE [PartDesign::Pocket] Pocket032
  BaseFeature = -> Pocket031
  Direction = (0,0,-1)
  Length = 5
  Length2 = 5
  Profile = -> Sketch038
  ReferenceAxis = -> Sketch038 [N_Axis]
  Type = 0
FEATURE [Sketcher::SketchObject] Sketch039
  ExternalGeometry = -> [Pocket032]
  FullyConstrained = true
  MapMode = 5
  Placement = pos=(0,-25,0) rot=(1,0,0;1.5708rad)
  Support = -> [Pocket032]
  sketch-geometry (2):
    g0: Circle CenterX=-20 CenterY=14 CenterZ=0 NormalX=0 NormalY=0 NormalZ=1 AngleXU=0 Radius=1.4
    g1: Circle CenterX=20 CenterY=14 CenterZ=0 NormalX=0 NormalY=0 NormalZ=1 AngleXU=0 Radius=1.4
  constraints (6):
    c: Diameter(g0) = 2.8
    c: Diameter(g1) = 2.8
    c: Distance(g0,g-5) = 5
    c: Distance(g0,g-3) = 6
    c: Distance(g1,g-3) = 6
    c: Distance(g1,g-4) = 5
FEATURE [PartDesign::Pocket] Pocket033
  BaseFeature = -> Pocket032
  Direction = (0,1,-2e-16)
  Length = 3
  Length2 = 5
  Profile = -> Sketch039
  ReferenceAxis = -> Sketch039 [N_Axis]
  Type = 0
FEATURE [PartDesign::Body] Body007  label="BackplaneBlock005"
  Group = -> [Sketch034,Pad006,Sketch035,Pocket029,Sketch036,Sketch037,Pocket030,Pocket031,Sketch038,Pocket032,Sketch039,Pocket033]
  Origin = -> Origin007
  Placement = pos=(85,25,0) rot=(0,0,1;0rad)
  Tip = -> Pocket033
FEATURE [Sketcher::SketchObject] Sketch040
  ExternalGeometry = -> [Pocket013]
  FullyConstrained = true
  MapMode = 5
  Placement = pos=(-25,0,0) rot=(0.57735,-0.57735,-0.57735;2.0944rad)
  Support = -> [Pocket013]
  sketch-geometry (2):
    g0: Circle CenterX=-20 CenterY=14 CenterZ=0 NormalX=0 NormalY=0 NormalZ=1 AngleXU=0 Radius=1.4
    g1: Circle CenterX=20 CenterY=14 CenterZ=0 NormalX=0 NormalY=0 NormalZ=1 AngleXU=0 Radius=1.4
  constraints (6):
    c: Diameter(g0) = 2.8
    c: Diameter(g1) = 2.8
    c: Distance(g0,g-3) = 5
    c: Distance(g0,g-4) = 6
    c: Distance(g1,g-4) = 6
    c: Distance(g1,g-5) = 5
FEATURE [PartDesign::Pocket] Pocket034
  BaseFeature = -> Pocket013
  Direction = (1,0,0)
  Length = 3
  Length2 = 5
  Profile = -> Sketch040
  ReferenceAxis = -> Sketch040 [N_Axis]
  Type = 0
FEATURE [PartDesign::Body] Body002  label="BackplaneBlock"
  Group = -> [Sketch002,Pad001,Sketch003,Pocket001,Sketch004,Sketch005,Pocket002,Pocket003,Sketch009,Pocket008,Sketch015,Pocket013,Sketch040,Pocket034]
  Origin = -> Origin002
  Placement = pos=(25,25,0) rot=(0,0,1;0rad)
  Tip = -> Pocket034
FEATURE [Sketcher::SketchObject] Sketch041
  FullyConstrained = true
  MapMode = 5
  Support = -> [XY_Plane008]
  sketch-geometry (4):
    g0: LineSegment StartX=-25 StartY=25 StartZ=0 EndX=25 EndY=25 EndZ=0
    g1: LineSegment StartX=25 StartY=25 StartZ=0 EndX=25 EndY=-25 EndZ=0
    g2: LineSegment StartX=25 StartY=-25 StartZ=0 EndX=-25 EndY=-25 EndZ=0
    g3: LineSegment StartX=-25 StartY=-25 StartZ=0 EndX=-25 EndY=25 EndZ=0
  constraints (10):
    c: Coincident(g0,g1)
    c: Coincident(g1,g2)
    c: Coincident(g2,g3)
    c: Coincident(g3,g0)
    c: Horizontal(g0)
    c: Vertical(g3)
    c: Symmetric(g2,g1,g-2)
    c: Symmetric(g1,g0,g-1)
    c: DistanceY(g1,g1) = 50
    c: DistanceX(g2,g2) = 50
FEATURE [PartDesign::Pad] Pad007
  Direction = (0,0,1)
  Length = 20
  Length2 = 10
  Profile = -> Sketch041
  ReferenceAxis = -> Sketch041 [N_Axis]
  Type = 0
FEATURE [Sketcher::SketchObject] Sketch042
  ExternalGeometry = -> [Pad007]
  FullyConstrained = true
  MapMode = 5
  Placement = pos=(0,0,20) rot=(0,0,1;0rad)
  Support = -> [Pad007]
  sketch-geometry (36):
    g0: LineSegment StartX=-18 StartY=15 StartZ=0 EndX=-17 EndY=15 EndZ=0
    g1: LineSegment StartX=20 StartY=13 StartZ=0 EndX=20 EndY=-13 EndZ=0
    g2: LineSegment StartX=18 StartY=-15 StartZ=0 EndX=17 EndY=-15 EndZ=0
    g3: LineSegment StartX=-20 StartY=-13 StartZ=0 EndX=-20 EndY=13 EndZ=0
    g4: LineSegment StartX=-13 StartY=20 StartZ=0 EndX=13 EndY=20 EndZ=0
    g5: LineSegment StartX=15 StartY=18 StartZ=0 EndX=15 EndY=17 EndZ=0
    g6: LineSegment StartX=13 StartY=-20 StartZ=0 EndX=-13 EndY=-20 EndZ=0
    g7: LineSegment StartX=-15 StartY=-18 StartZ=0 EndX=-15 EndY=-17 EndZ=0
    g8: LineSegment StartX=17 StartY=15 StartZ=0 EndX=18 EndY=15 EndZ=0
    g9: LineSegment StartX=-15 StartY=17 StartZ=0 EndX=-15 EndY=18 EndZ=0
    g10: LineSegment StartX=-17 StartY=-15 StartZ=0 EndX=-18 EndY=-15 EndZ=0
    g11: LineSegment StartX=15 StartY=-17 StartZ=0 EndX=15 EndY=-18 EndZ=0
    g12: ArcOfCircle CenterX=-13 CenterY=-18 CenterZ=0 NormalX=0 NormalY=0 NormalZ=1 AngleXU=0 Radius=2 StartAngle=3.14159 EndAngle=4.71239
    g13: GeomPoint X=-15 Y=-20 Z=0
    g14: ArcOfCircle CenterX=13 CenterY=-18 CenterZ=0 NormalX=0 NormalY=0 NormalZ=1 AngleXU=0 Radius=2 StartAngle=4.71239 EndAngle=6.28319
    g15: GeomPoint X=15 Y=-20 Z=0
    g16: ArcOfCircle CenterX=17 CenterY=-17 CenterZ=0 NormalX=0 NormalY=0 NormalZ=1 AngleXU=0 Radius=2 StartAngle=1.5708 EndAngle=3.14159
    g17: GeomPoint X=15 Y=-15 Z=0
    g18: ArcOfCircle CenterX=18 CenterY=-13 CenterZ=0 NormalX=0 NormalY=0 NormalZ=1 AngleXU=0 Radius=2 StartAngle=4.71239 EndAngle=6.28319
    g19: GeomPoint X=20 Y=-15 Z=0
    g20: ArcOfCircle CenterX=18 CenterY=13 CenterZ=0 NormalX=0 NormalY=0 NormalZ=1 AngleXU=0 Radius=2 StartAngle=0 EndAngle=1.5708
    g21: GeomPoint X=20 Y=15 Z=0
    g22: ArcOfCircle CenterX=17 CenterY=17 CenterZ=0 NormalX=0 NormalY=0 NormalZ=1 AngleXU=0 Radius=2 StartAngle=3.14159 EndAngle=4.71239
    g23: GeomPoint X=15 Y=15 Z=0
    g24: ArcOfCircle CenterX=13 CenterY=18 CenterZ=0 NormalX=0 NormalY=0 NormalZ=1 AngleXU=0 Radius=2 StartAngle=4e-16 EndAngle=1.5708
    g25: GeomPoint X=15 Y=20 Z=0
    g26: ArcOfCircle CenterX=-13 CenterY=18 CenterZ=0 NormalX=0 NormalY=0 NormalZ=1 AngleXU=0 Radius=2 StartAngle=1.5708 EndAngle=3.14159
    g27: GeomPoint X=-15 Y=20 Z=0
    g28: ArcOfCircle CenterX=-17 CenterY=17 CenterZ=0 NormalX=0 NormalY=0 NormalZ=1 AngleXU=0 Radius=2 StartAngle=4.71239 EndAngle=6.28319
    g29: GeomPoint X=-15 Y=15 Z=0
    g30: ArcOfCircle CenterX=-18 CenterY=13 CenterZ=0 NormalX=0 NormalY=0 NormalZ=1 AngleXU=0 Radius=2 StartAngle=1.5708 EndAngle=3.14159
    g31: GeomPoint X=-20 Y=15 Z=0
    g32: ArcOfCircle CenterX=-18 CenterY=-13 CenterZ=0 NormalX=0 NormalY=0 NormalZ=1 AngleXU=0 Radius=2 StartAngle=3.14159 EndAngle=4.71239
    g33: GeomPoint X=-20 Y=-15 Z=0
    g34: ArcOfCircle CenterX=-17 CenterY=-17 CenterZ=0 NormalX=0 NormalY=0 NormalZ=1 AngleXU=0 Radius=2 StartAngle=0 EndAngle=1.5708
    g35: GeomPoint X=-15 Y=-15 Z=0
  constraints (80):
    c: Horizontal(g2)
    c: Vertical(g3)
    c: Symmetric(g21,g31,g-2)
    c: Symmetric(g21,g19,g-1)
    c: DistanceX(g31,g21) = 40
    c: DistanceY(g19,g21) = 30
    c: Horizontal(g4)
    c: Vertical(g7)
    c: Symmetric(g13,g15,g-2)
    c: Symmetric(g15,g25,g-1)
    c: DistanceY(g15,g25) = 40
    c: Vertical(g9)
    c: Vertical(g5)
    c: Vertical(g11)
    c: Horizontal(g10)
    c: Horizontal(g8)
    c: Horizontal(g0)
    c: DistanceX(g13,g15) = 30
    c: DistanceY(g33,g31) = 30
    c: DistanceX(g27,g25) = 30
    c: PointOnObject(g13,g7)
    c: PointOnObject(g13,g6)
    c: Tangent(g7,g12) = 1.5708
    c: Tangent(g6,g12) = 1.5708
    c: Radius(g12) = 2
    c: PointOnObject(g15,g11)
    c: PointOnObject(g15,g6)
    c: Tangent(g11,g14) = 1.5708
    c: Tangent(g6,g14) = 1.5708
    c: PointOnObject(g17,g11)
    c: PointOnObject(g17,g2)
    c: Tangent(g11,g16) = -1.5708
    c: Tangent(g2,g16) = -1.5708
    c: PointOnObject(g19,g2)
    c: PointOnObject(g19,g1)
    c: Tangent(g2,g18) = 1.5708
    c: Tangent(g1,g18) = 1.5708
    c: PointOnObject(g21,g1)
    c: PointOnObject(g21,g8)
    c: Tangent(g1,g20) = 1.5708
    c: Tangent(g8,g20) = 1.5708
    c: PointOnObject(g23,g8)
    c: PointOnObject(g23,g5)
    c: Tangent(g8,g22) = -1.5708
    c: Tangent(g5,g22) = -1.5708
    c: PointOnObject(g25,g5)
    c: PointOnObject(g25,g4)
    c: Tangent(g5,g24) = 1.5708
    c: Tangent(g4,g24) = 1.5708
    c: PointOnObject(g27,g9)
    c: PointOnObject(g27,g4)
    c: Tangent(g9,g26) = 1.5708
    c: Tangent(g4,g26) = 1.5708
    c: PointOnObject(g29,g9)
    c: PointOnObject(g29,g0)
    c: Tangent(g9,g28) = -1.5708
    c: Tangent(g0,g28) = -1.5708
    c: PointOnObject(g31,g0)
    c: PointOnObject(g31,g3)
    c: Tangent(g0,g30) = 1.5708
    c: Tangent(g3,g30) = 1.5708
    c: PointOnObject(g33,g3)
    c: PointOnObject(g33,g10)
    c: Tangent(g3,g32) = 1.5708
    c: Tangent(g10,g32) = 1.5708
    c: PointOnObject(g35,g10)
    c: PointOnObject(g35,g7)
    c: Tangent(g10,g34) = -1.5708
    c: Tangent(g7,g34) = -1.5708
    c: Radius(g34) = 2
    c: Radius(g32) = 2
    c: Radius(g30) = 2
    c: Radius(g28) = 2
    c: Radius(g26) = 2
    c: Radius(g24) = 2
    c: Radius(g22) = 2
    c: Radius(g20) = 2
    c: Radius(g18) = 2
    c: Radius(g16) = 2
    c: Radius(g14) = 2
FEATURE [PartDesign::Pocket] Pocket035
  BaseFeature = -> Pad007
  Direction = (0,0,-1)
  Length = 5
  Length2 = 5
  Profile = -> Sketch042
  ReferenceAxis = -> Sketch042 [N_Axis]
  Type = 1
FEATURE [Sketcher::SketchObject] Sketch043
  ExternalGeometry = -> [Pocket035]
  FullyConstrained = true
  MapMode = 5
  Placement = pos=(25,0,0) rot=(0.57735,0.57735,0.57735;2.0944rad)
  Support = -> [Pocket035]
  sketch-geometry (6):
    g0: LineSegment StartX=-15 StartY=10 StartZ=0 EndX=15 EndY=10 EndZ=0
    g1: LineSegment StartX=20 StartY=5 StartZ=0 EndX=20 EndY=0 EndZ=0
    g2: LineSegment StartX=20 StartY=0 StartZ=0 EndX=-20 EndY=0 EndZ=0
    g3: LineSegment StartX=-20 StartY=0 StartZ=0 EndX=-20 EndY=5 EndZ=0
    g4: ArcOfCircle CenterX=15 CenterY=5 CenterZ=0 NormalX=0 NormalY=0 NormalZ=1 AngleXU=0 Radius=5 StartAngle=1.11001e-11 EndAngle=1.5708
    g5: ArcOfCircle CenterX=-15 CenterY=5 CenterZ=0 NormalX=0 NormalY=0 NormalZ=1 AngleXU=0 Radius=5 StartAngle=1.5708 EndAngle=3.14159
  constraints (15):
    c: Coincident(g1,g2)
    c: Coincident(g2,g3)
    c: Vertical(g1)
    c: Vertical(g3)
    c: PointOnObject(g1,g-1)
    c: Tangent(g1,g4) = 1.5708
    c: Tangent(g0,g4) = 1.5708
    c: Tangent(g0,g5) = 1.5708
    c: Tangent(g3,g5) = 1.5708
    c: Horizontal(g0)
    c: DistanceX(g2,g2) = 40
    c: Symmetric(g2,g1,g-2)
    c: Distance(g-1,g0) = 10
    c: Radius(g5) = 5
    c: Radius(g4) = 5
FEATURE [PartDesign::Pocket] Pocket036
  BaseFeature = -> Pocket035
  Direction = (-1,0,0)
  Length = 5
  Length2 = 5
  Profile = -> Sketch043
  ReferenceAxis = -> Sketch043 [N_Axis]
  Type = 1
FEATURE [Sketcher::SketchObject] Sketch044
  FullyConstrained = true
  MapMode = 5
  Placement = pos=(0,-25,0) rot=(1,0,0;1.5708rad)
  Support = -> [Pocket035]
  sketch-geometry (6):
    g0: LineSegment StartX=-15 StartY=10 StartZ=0 EndX=15 EndY=10 EndZ=0
    g1: LineSegment StartX=20 StartY=5 StartZ=0 EndX=20 EndY=0 EndZ=0
    g2: LineSegment StartX=20 StartY=0 StartZ=0 EndX=-20 EndY=0 EndZ=0
    g3: LineSegment StartX=-20 StartY=0 StartZ=0 EndX=-20 EndY=5 EndZ=0
    g4: ArcOfCircle CenterX=15 CenterY=5 CenterZ=0 NormalX=0 NormalY=0 NormalZ=1 AngleXU=0 Radius=5 StartAngle=1.11e-11 EndAngle=1.5708
    g5: ArcOfCircle CenterX=-15 CenterY=5 CenterZ=0 NormalX=0 NormalY=0 NormalZ=1 AngleXU=0 Radius=5 StartAngle=1.5708 EndAngle=3.14159
  constraints (15):
    c: Coincident(g1,g2)
    c: Coincident(g2,g3)
    c: Horizontal(g0)
    c: Vertical(g1)
    c: Vertical(g3)
    c: Symmetric(g2,g1,g-2)
    c: PointOnObject(g1,g-1)
    c: Tangent(g0,g4) = 1.5708
    c: Tangent(g1,g4) = 1.5708
    c: Tangent(g0,g5) = 1.5708
    c: Tangent(g3,g5) = 1.5708
    c: DistanceX(g2,g2) = 40
    c: Distance(g-1,g0) = 10
    c: Radius(g5) = 5
    c: Radius(g4) = 5
FEATURE [PartDesign::Pocket] Pocket037
  BaseFeature = -> Pocket036
  Direction = (0,1,-2e-16)
  Length = 5
  Length2 = 5
  Profile = -> Sketch044
  ReferenceAxis = -> Sketch044 [N_Axis]
  Type = 1
FEATURE [Sketcher::SketchObject] Sketch045
  FullyConstrained = false
  MapMode = 5
  Placement = pos=(0,0,20) rot=(0,0,1;0rad)
  sketch-geometry (4):
    g0: Circle CenterX=-20 CenterY=20 CenterZ=0 NormalX=0 NormalY=0 NormalZ=1 AngleXU=0 Radius=1.55
    g1: Circle CenterX=20 CenterY=20 CenterZ=0 NormalX=0 NormalY=0 NormalZ=1 AngleXU=0 Radius=1.55
    g2: Circle CenterX=20 CenterY=-20 CenterZ=0 NormalX=0 NormalY=0 NormalZ=1 AngleXU=0 Radius=1.55
    g3: Circle CenterX=-20 CenterY=-20 CenterZ=0 NormalX=0 NormalY=0 NormalZ=1 AngleXU=0 Radius=1.55
  constraints (4):
    c: Diameter(g0) = 3.1
    c: Diameter(g1) = 3.1
    c: Diameter(g2) = 3.1
    c: Diameter(g3) = 3.1
FEATURE [PartDesign::Pocket] Pocket038
  BaseFeature = -> Pocket037
  Direction = (0,0,-1)
  Length = 5
  Length2 = 5
  Profile = -> Sketch045
  ReferenceAxis = -> Sketch045 [N_Axis]
  Type = 0
FEATURE [Sketcher::SketchObject] Sketch046
  ExternalGeometry = -> [Pocket038]
  FullyConstrained = true
  MapMode = 5
  Placement = pos=(0,-25,0) rot=(1,0,0;1.5708rad)
  Support = -> [Pocket038]
  sketch-geometry (2):
    g0: Circle CenterX=-20 CenterY=14 CenterZ=0 NormalX=0 NormalY=0 NormalZ=1 AngleXU=0 Radius=1.55
    g1: Circle CenterX=20 CenterY=14 CenterZ=0 NormalX=0 NormalY=0 NormalZ=1 AngleXU=0 Radius=1.55
  constraints (6):
    c: Diameter(g0) = 3.1
    c: Diameter(g1) = 3.1
    c: Distance(g0,g-5) = 5
    c: Distance(g0,g-3) = 6
    c: Distance(g1,g-3) = 6
    c: Distance(g1,g-4) = 5
FEATURE [PartDesign::Pocket] Pocket039
  BaseFeature = -> Pocket038
  Direction = (0,1,-2e-16)
  Length = 3
  Length2 = 5
  Profile = -> Sketch046
  ReferenceAxis = -> Sketch046 [N_Axis]
  Type = 0
FEATURE [Sketcher::SketchObject] Sketch047
  ExternalGeometry = -> [Pocket039]
  FullyConstrained = true
  MapMode = 5
  Placement = pos=(-25,0,0) rot=(0.57735,-0.57735,-0.57735;2.0944rad)
  Support = -> [Pocket039]
  sketch-geometry (2):
    g0: Circle CenterX=-20 CenterY=14 CenterZ=0 NormalX=0 NormalY=0 NormalZ=1 AngleXU=0 Radius=1.4
    g1: Circle CenterX=20 CenterY=14 CenterZ=0 NormalX=0 NormalY=0 NormalZ=1 AngleXU=0 Radius=1.4
  constraints (6):
    c: Diameter(g0) = 2.8
    c: Diameter(g1) = 2.8
    c: Distance(g0,g-3) = 5
    c: Distance(g0,g-4) = 6
    c: Distance(g1,g-4) = 6
    c: Distance(g1,g-5) = 5
FEATURE [PartDesign::Pocket] Pocket040
  BaseFeature = -> Pocket039
  Direction = (1,0,0)
  Length = 3
  Length2 = 5
  Profile = -> Sketch047
  ReferenceAxis = -> Sketch047 [N_Axis]
  Type = 0
FEATURE [PartDesign::Body] Body008  label="BackplaneBlock006"
  Group = -> [Sketch041,Pad007,Sketch042,Pocket035,Sketch043,Sketch044,Pocket036,Pocket037,Sketch045,Pocket038,Sketch046,Pocket039,Sketch047,Pocket040]
  Origin = -> Origin008
  Placement = pos=(145,25,0) rot=(0,0,1;1.5708rad)
  Tip = -> Pocket040
FEATURE [Sketcher::SketchObject] Sketch048
  FullyConstrained = true
  MapMode = 5
  Support = -> [XY_Plane009]
  sketch-geometry (4):
    g0: LineSegment StartX=-25 StartY=25 StartZ=0 EndX=25 EndY=25 EndZ=0
    g1: LineSegment StartX=25 StartY=25 StartZ=0 EndX=25 EndY=-25 EndZ=0
    g2: LineSegment StartX=25 StartY=-25 StartZ=0 EndX=-25 EndY=-25 EndZ=0
    g3: LineSegment StartX=-25 StartY=-25 StartZ=0 EndX=-25 EndY=25 EndZ=0
  constraints (10):
    c: Coincident(g0,g1)
    c: Coincident(g1,g2)
    c: Coincident(g2,g3)
    c: Coincident(g3,g0)
    c: Horizontal(g0)
    c: Vertical(g3)
    c: Symmetric(g2,g1,g-2)
    c: Symmetric(g1,g0,g-1)
    c: DistanceY(g1,g1) = 50
    c: DistanceX(g2,g2) = 50
FEATURE [PartDesign::Pad] Pad008
  Direction = (0,0,1)
  Length = 20
  Length2 = 10
  Profile = -> Sketch048
  ReferenceAxis = -> Sketch048 [N_Axis]
  Type = 0
FEATURE [Sketcher::SketchObject] Sketch049
  ExternalGeometry = -> [Pad008]
  FullyConstrained = true
  MapMode = 5
  Placement = pos=(0,0,20) rot=(0,0,1;0rad)
  Support = -> [Pad008]
  sketch-geometry (36):
    g0: LineSegment StartX=-18 StartY=15 StartZ=0 EndX=-17 EndY=15 EndZ=0
    g1: LineSegment StartX=20 StartY=13 StartZ=0 EndX=20 EndY=-13 EndZ=0
    g2: LineSegment StartX=18 StartY=-15 StartZ=0 EndX=17 EndY=-15 EndZ=0
    g3: LineSegment StartX=-20 StartY=-13 StartZ=0 EndX=-20 EndY=13 EndZ=0
    g4: LineSegment StartX=-13 StartY=20 StartZ=0 EndX=13 EndY=20 EndZ=0
    g5: LineSegment StartX=15 StartY=18 StartZ=0 EndX=15 EndY=17 EndZ=0
    g6: LineSegment StartX=13 StartY=-20 StartZ=0 EndX=-13 EndY=-20 EndZ=0
    g7: LineSegment StartX=-15 StartY=-18 StartZ=0 EndX=-15 EndY=-17 EndZ=0
    g8: LineSegment StartX=17 StartY=15 StartZ=0 EndX=18 EndY=15 EndZ=0
    g9: LineSegment StartX=-15 StartY=17 StartZ=0 EndX=-15 EndY=18 EndZ=0
    g10: LineSegment StartX=-17 StartY=-15 StartZ=0 EndX=-18 EndY=-15 EndZ=0
    g11: LineSegment StartX=15 StartY=-17 StartZ=0 EndX=15 EndY=-18 EndZ=0
    g12: ArcOfCircle CenterX=-13 CenterY=-18 CenterZ=0 NormalX=0 NormalY=0 NormalZ=1 AngleXU=0 Radius=2 StartAngle=3.14159 EndAngle=4.71239
    g13: GeomPoint X=-15 Y=-20 Z=0
    g14: ArcOfCircle CenterX=13 CenterY=-18 CenterZ=0 NormalX=0 NormalY=0 NormalZ=1 AngleXU=0 Radius=2 StartAngle=4.71239 EndAngle=6.28319
    g15: GeomPoint X=15 Y=-20 Z=0
    g16: ArcOfCircle CenterX=17 CenterY=-17 CenterZ=0 NormalX=0 NormalY=0 NormalZ=1 AngleXU=0 Radius=2 StartAngle=1.5708 EndAngle=3.14159
    g17: GeomPoint X=15 Y=-15 Z=0
    g18: ArcOfCircle CenterX=18 CenterY=-13 CenterZ=0 NormalX=0 NormalY=0 NormalZ=1 AngleXU=0 Radius=2 StartAngle=4.71239 EndAngle=6.28319
    g19: GeomPoint X=20 Y=-15 Z=0
    g20: ArcOfCircle CenterX=18 CenterY=13 CenterZ=0 NormalX=0 NormalY=0 NormalZ=1 AngleXU=0 Radius=2 StartAngle=0 EndAngle=1.5708
    g21: GeomPoint X=20 Y=15 Z=0
    g22: ArcOfCircle CenterX=17 CenterY=17 CenterZ=0 NormalX=0 NormalY=0 NormalZ=1 AngleXU=0 Radius=2 StartAngle=3.14159 EndAngle=4.71239
    g23: GeomPoint X=15 Y=15 Z=0
    g24: ArcOfCircle CenterX=13 CenterY=18 CenterZ=0 NormalX=0 NormalY=0 NormalZ=1 AngleXU=0 Radius=2 StartAngle=4e-16 EndAngle=1.5708
    g25: GeomPoint X=15 Y=20 Z=0
    g26: ArcOfCircle CenterX=-13 CenterY=18 CenterZ=0 NormalX=0 NormalY=0 NormalZ=1 AngleXU=0 Radius=2 StartAngle=1.5708 EndAngle=3.14159
    g27: GeomPoint X=-15 Y=20 Z=0
    g28: ArcOfCircle CenterX=-17 CenterY=17 CenterZ=0 NormalX=0 NormalY=0 NormalZ=1 AngleXU=0 Radius=2 StartAngle=4.71239 EndAngle=6.28319
    g29: GeomPoint X=-15 Y=15 Z=0
    g30: ArcOfCircle CenterX=-18 CenterY=13 CenterZ=0 NormalX=0 NormalY=0 NormalZ=1 AngleXU=0 Radius=2 StartAngle=1.5708 EndAngle=3.14159
    g31: GeomPoint X=-20 Y=15 Z=0
    g32: ArcOfCircle CenterX=-18 CenterY=-13 CenterZ=0 NormalX=0 NormalY=0 NormalZ=1 AngleXU=0 Radius=2 StartAngle=3.14159 EndAngle=4.71239
    g33: GeomPoint X=-20 Y=-15 Z=0
    g34: ArcOfCircle CenterX=-17 CenterY=-17 CenterZ=0 NormalX=0 NormalY=0 NormalZ=1 AngleXU=0 Radius=2 StartAngle=0 EndAngle=1.5708
    g35: GeomPoint X=-15 Y=-15 Z=0
  constraints (80):
    c: Horizontal(g2)
    c: Vertical(g3)
    c: Symmetric(g21,g31,g-2)
    c: Symmetric(g21,g19,g-1)
    c: DistanceX(g31,g21) = 40
    c: DistanceY(g19,g21) = 30
    c: Horizontal(g4)
    c: Vertical(g7)
    c: Symmetric(g13,g15,g-2)
    c: Symmetric(g15,g25,g-1)
    c: DistanceY(g15,g25) = 40
    c: Vertical(g9)
    c: Vertical(g5)
    c: Vertical(g11)
    c: Horizontal(g10)
    c: Horizontal(g8)
    c: Horizontal(g0)
    c: DistanceX(g13,g15) = 30
    c: DistanceY(g33,g31) = 30
    c: DistanceX(g27,g25) = 30
    c: PointOnObject(g13,g7)
    c: PointOnObject(g13,g6)
    c: Tangent(g7,g12) = 1.5708
    c: Tangent(g6,g12) = 1.5708
    c: Radius(g12) = 2
    c: PointOnObject(g15,g11)
    c: PointOnObject(g15,g6)
    c: Tangent(g11,g14) = 1.5708
    c: Tangent(g6,g14) = 1.5708
    c: PointOnObject(g17,g11)
    c: PointOnObject(g17,g2)
    c: Tangent(g11,g16) = -1.5708
    c: Tangent(g2,g16) = -1.5708
    c: PointOnObject(g19,g2)
    c: PointOnObject(g19,g1)
    c: Tangent(g2,g18) = 1.5708
    c: Tangent(g1,g18) = 1.5708
    c: PointOnObject(g21,g1)
    c: PointOnObject(g21,g8)
    c: Tangent(g1,g20) = 1.5708
    c: Tangent(g8,g20) = 1.5708
    c: PointOnObject(g23,g8)
    c: PointOnObject(g23,g5)
    c: Tangent(g8,g22) = -1.5708
    c: Tangent(g5,g22) = -1.5708
    c: PointOnObject(g25,g5)
    c: PointOnObject(g25,g4)
    c: Tangent(g5,g24) = 1.5708
    c: Tangent(g4,g24) = 1.5708
    c: PointOnObject(g27,g9)
    c: PointOnObject(g27,g4)
    c: Tangent(g9,g26) = 1.5708
    c: Tangent(g4,g26) = 1.5708
    c: PointOnObject(g29,g9)
    c: PointOnObject(g29,g0)
    c: Tangent(g9,g28) = -1.5708
    c: Tangent(g0,g28) = -1.5708
    c: PointOnObject(g31,g0)
    c: PointOnObject(g31,g3)
    c: Tangent(g0,g30) = 1.5708
    c: Tangent(g3,g30) = 1.5708
    c: PointOnObject(g33,g3)
    c: PointOnObject(g33,g10)
    c: Tangent(g3,g32) = 1.5708
    c: Tangent(g10,g32) = 1.5708
    c: PointOnObject(g35,g10)
    c: PointOnObject(g35,g7)
    c: Tangent(g10,g34) = -1.5708
    c: Tangent(g7,g34) = -1.5708
    c: Radius(g34) = 2
    c: Radius(g32) = 2
    c: Radius(g30) = 2
    c: Radius(g28) = 2
    c: Radius(g26) = 2
    c: Radius(g24) = 2
    c: Radius(g22) = 2
    c: Radius(g20) = 2
    c: Radius(g18) = 2
    c: Radius(g16) = 2
    c: Radius(g14) = 2
FEATURE [PartDesign::Pocket] Pocket041
  BaseFeature = -> Pad008
  Direction = (0,0,-1)
  Length = 5
  Length2 = 5
  Profile = -> Sketch049
  ReferenceAxis = -> Sketch049 [N_Axis]
  Type = 1
FEATURE [Sketcher::SketchObject] Sketch050
  ExternalGeometry = -> [Pocket041]
  FullyConstrained = true
  MapMode = 5
  Placement = pos=(25,0,0) rot=(0.57735,0.57735,0.57735;2.0944rad)
  Support = -> [Pocket041]
  sketch-geometry (6):
    g0: LineSegment StartX=-15 StartY=10 StartZ=0 EndX=15 EndY=10 EndZ=0
    g1: LineSegment StartX=20 StartY=5 StartZ=0 EndX=20 EndY=0 EndZ=0
    g2: LineSegment StartX=20 StartY=0 StartZ=0 EndX=-20 EndY=0 EndZ=0
    g3: LineSegment StartX=-20 StartY=0 StartZ=0 EndX=-20 EndY=5 EndZ=0
    g4: ArcOfCircle CenterX=15 CenterY=5 CenterZ=0 NormalX=0 NormalY=0 NormalZ=1 AngleXU=0 Radius=5 StartAngle=1.11001e-11 EndAngle=1.5708
    g5: ArcOfCircle CenterX=-15 CenterY=5 CenterZ=0 NormalX=0 NormalY=0 NormalZ=1 AngleXU=0 Radius=5 StartAngle=1.5708 EndAngle=3.14159
  constraints (15):
    c: Coincident(g1,g2)
    c: Coincident(g2,g3)
    c: Vertical(g1)
    c: Vertical(g3)
    c: PointOnObject(g1,g-1)
    c: Tangent(g1,g4) = 1.5708
    c: Tangent(g0,g4) = 1.5708
    c: Tangent(g0,g5) = 1.5708
    c: Tangent(g3,g5) = 1.5708
    c: Horizontal(g0)
    c: DistanceX(g2,g2) = 40
    c: Symmetric(g2,g1,g-2)
    c: Distance(g-1,g0) = 10
    c: Radius(g5) = 5
    c: Radius(g4) = 5
FEATURE [PartDesign::Pocket] Pocket042
  BaseFeature = -> Pocket041
  Direction = (-1,0,0)
  Length = 5
  Length2 = 5
  Profile = -> Sketch050
  ReferenceAxis = -> Sketch050 [N_Axis]
  Type = 1
FEATURE [Sketcher::SketchObject] Sketch051
  FullyConstrained = true
  MapMode = 5
  Placement = pos=(0,-25,0) rot=(1,0,0;1.5708rad)
  Support = -> [Pocket041]
  sketch-geometry (6):
    g0: LineSegment StartX=-15 StartY=10 StartZ=0 EndX=15 EndY=10 EndZ=0
    g1: LineSegment StartX=20 StartY=5 StartZ=0 EndX=20 EndY=0 EndZ=0
    g2: LineSegment StartX=20 StartY=0 StartZ=0 EndX=-20 EndY=0 EndZ=0
    g3: LineSegment StartX=-20 StartY=0 StartZ=0 EndX=-20 EndY=5 EndZ=0
    g4: ArcOfCircle CenterX=15 CenterY=5 CenterZ=0 NormalX=0 NormalY=0 NormalZ=1 AngleXU=0 Radius=5 StartAngle=1.11e-11 EndAngle=1.5708
    g5: ArcOfCircle CenterX=-15 CenterY=5 CenterZ=0 NormalX=0 NormalY=0 NormalZ=1 AngleXU=0 Radius=5 StartAngle=1.5708 EndAngle=3.14159
  constraints (15):
    c: Coincident(g1,g2)
    c: Coincident(g2,g3)
    c: Horizontal(g0)
    c: Vertical(g1)
    c: Vertical(g3)
    c: Symmetric(g2,g1,g-2)
    c: PointOnObject(g1,g-1)
    c: Tangent(g0,g4) = 1.5708
    c: Tangent(g1,g4) = 1.5708
    c: Tangent(g0,g5) = 1.5708
    c: Tangent(g3,g5) = 1.5708
    c: DistanceX(g2,g2) = 40
    c: Distance(g-1,g0) = 10
    c: Radius(g5) = 5
    c: Radius(g4) = 5
FEATURE [PartDesign::Pocket] Pocket043
  BaseFeature = -> Pocket042
  Direction = (0,1,-2e-16)
  Length = 5
  Length2 = 5
  Profile = -> Sketch051
  ReferenceAxis = -> Sketch051 [N_Axis]
  Type = 1
FEATURE [Sketcher::SketchObject] Sketch052
  FullyConstrained = false
  MapMode = 5
  Placement = pos=(0,0,20) rot=(0,0,1;0rad)
  sketch-geometry (4):
    g0: Circle CenterX=-20 CenterY=20 CenterZ=0 NormalX=0 NormalY=0 NormalZ=1 AngleXU=0 Radius=1.55
    g1: Circle CenterX=20 CenterY=20 CenterZ=0 NormalX=0 NormalY=0 NormalZ=1 AngleXU=0 Radius=1.55
    g2: Circle CenterX=20 CenterY=-20 CenterZ=0 NormalX=0 NormalY=0 NormalZ=1 AngleXU=0 Radius=1.55
    g3: Circle CenterX=-20 CenterY=-20 CenterZ=0 NormalX=0 NormalY=0 NormalZ=1 AngleXU=0 Radius=1.55
  constraints (4):
    c: Diameter(g0) = 3.1
    c: Diameter(g1) = 3.1
    c: Diameter(g2) = 3.1
    c: Diameter(g3) = 3.1
FEATURE [PartDesign::Pocket] Pocket044
  BaseFeature = -> Pocket043
  Direction = (0,0,-1)
  Length = 5
  Length2 = 5
  Profile = -> Sketch052
  ReferenceAxis = -> Sketch052 [N_Axis]
  Type = 0
FEATURE [Sketcher::SketchObject] Sketch053
  ExternalGeometry = -> [Pocket044]
  FullyConstrained = true
  MapMode = 5
  Placement = pos=(0,-25,0) rot=(1,0,0;1.5708rad)
  Support = -> [Pocket044]
  sketch-geometry (2):
    g0: Circle CenterX=-20 CenterY=14 CenterZ=0 NormalX=0 NormalY=0 NormalZ=1 AngleXU=0 Radius=1.4
    g1: Circle CenterX=20 CenterY=14 CenterZ=0 NormalX=0 NormalY=0 NormalZ=1 AngleXU=0 Radius=1.4
  constraints (6):
    c: Diameter(g0) = 2.8
    c: Diameter(g1) = 2.8
    c: Distance(g0,g-5) = 5
    c: Distance(g0,g-3) = 6
    c: Distance(g1,g-3) = 6
    c: Distance(g1,g-4) = 5
FEATURE [PartDesign::Pocket] Pocket045
  BaseFeature = -> Pocket044
  Direction = (0,1,-2e-16)
  Length = 3
  Length2 = 5
  Profile = -> Sketch053
  ReferenceAxis = -> Sketch053 [N_Axis]
  Type = 0
FEATURE [Sketcher::SketchObject] Sketch054
  ExternalGeometry = -> [Pocket045]
  FullyConstrained = true
  MapMode = 5
  Placement = pos=(-25,0,0) rot=(0.57735,-0.57735,-0.57735;2.0944rad)
  Support = -> [Pocket045]
  sketch-geometry (2):
    g0: Circle CenterX=-20 CenterY=14 CenterZ=0 NormalX=0 NormalY=0 NormalZ=1 AngleXU=0 Radius=1.4
    g1: Circle CenterX=20 CenterY=14 CenterZ=0 NormalX=0 NormalY=0 NormalZ=1 AngleXU=0 Radius=1.4
  constraints (6):
    c: Diameter(g0) = 2.8
    c: Diameter(g1) = 2.8
    c: Distance(g0,g-3) = 5
    c: Distance(g0,g-4) = 6
    c: Distance(g1,g-4) = 6
    c: Distance(g1,g-5) = 5
FEATURE [PartDesign::Pocket] Pocket046
  BaseFeature = -> Pocket045
  Direction = (1,0,0)
  Length = 3
  Length2 = 5
  Profile = -> Sketch054
  ReferenceAxis = -> Sketch054 [N_Axis]
  Type = 0
FEATURE [PartDesign::Body] Body009  label="BackplaneBlock007"
  Group = -> [Sketch048,Pad008,Sketch049,Pocket041,Sketch050,Sketch051,Pocket042,Pocket043,Sketch052,Pocket044,Sketch053,Pocket045,Sketch054,Pocket046]
  Origin = -> Origin009
  Placement = pos=(25,145,0) rot=(0,0,-1;1.5708rad)
  Tip = -> Pocket046
FEATURE [Sketcher::SketchObject] Sketch055
  FullyConstrained = true
  MapMode = 5
  Support = -> [XY_Plane010]
  sketch-geometry (4):
    g0: LineSegment StartX=-25 StartY=25 StartZ=0 EndX=25 EndY=25 EndZ=0
    g1: LineSegment StartX=25 StartY=25 StartZ=0 EndX=25 EndY=-25 EndZ=0
    g2: LineSegment StartX=25 StartY=-25 StartZ=0 EndX=-25 EndY=-25 EndZ=0
    g3: LineSegment StartX=-25 StartY=-25 StartZ=0 EndX=-25 EndY=25 EndZ=0
  constraints (10):
    c: Coincident(g0,g1)
    c: Coincident(g1,g2)
    c: Coincident(g2,g3)
    c: Coincident(g3,g0)
    c: Horizontal(g0)
    c: Vertical(g3)
    c: Symmetric(g2,g1,g-2)
    c: Symmetric(g1,g0,g-1)
    c: DistanceY(g1,g1) = 50
    c: DistanceX(g2,g2) = 50
FEATURE [PartDesign::Pad] Pad009
  Direction = (0,0,1)
  Length = 20
  Length2 = 10
  Profile = -> Sketch055
  ReferenceAxis = -> Sketch055 [N_Axis]
  Type = 0
FEATURE [Sketcher::SketchObject] Sketch056
  ExternalGeometry = -> [Pad009]
  FullyConstrained = true
  MapMode = 5
  Placement = pos=(0,0,20) rot=(0,0,1;0rad)
  Support = -> [Pad009]
  sketch-geometry (36):
    g0: LineSegment StartX=-18 StartY=15 StartZ=0 EndX=-17 EndY=15 EndZ=0
    g1: LineSegment StartX=20 StartY=13 StartZ=0 EndX=20 EndY=-13 EndZ=0
    g2: LineSegment StartX=18 StartY=-15 StartZ=0 EndX=17 EndY=-15 EndZ=0
    g3: LineSegment StartX=-20 StartY=-13 StartZ=0 EndX=-20 EndY=13 EndZ=0
    g4: LineSegment StartX=-13 StartY=20 StartZ=0 EndX=13 EndY=20 EndZ=0
    g5: LineSegment StartX=15 StartY=18 StartZ=0 EndX=15 EndY=17 EndZ=0
    g6: LineSegment StartX=13 StartY=-20 StartZ=0 EndX=-13 EndY=-20 EndZ=0
    g7: LineSegment StartX=-15 StartY=-18 StartZ=0 EndX=-15 EndY=-17 EndZ=0
    g8: LineSegment StartX=17 StartY=15 StartZ=0 EndX=18 EndY=15 EndZ=0
    g9: LineSegment StartX=-15 StartY=17 StartZ=0 EndX=-15 EndY=18 EndZ=0
    g10: LineSegment StartX=-17 StartY=-15 StartZ=0 EndX=-18 EndY=-15 EndZ=0
    g11: LineSegment StartX=15 StartY=-17 StartZ=0 EndX=15 EndY=-18 EndZ=0
    g12: ArcOfCircle CenterX=-13 CenterY=-18 CenterZ=0 NormalX=0 NormalY=0 NormalZ=1 AngleXU=0 Radius=2 StartAngle=3.14159 EndAngle=4.71239
    g13: GeomPoint X=-15 Y=-20 Z=0
    g14: ArcOfCircle CenterX=13 CenterY=-18 CenterZ=0 NormalX=0 NormalY=0 NormalZ=1 AngleXU=0 Radius=2 StartAngle=4.71239 EndAngle=6.28319
    g15: GeomPoint X=15 Y=-20 Z=0
    g16: ArcOfCircle CenterX=17 CenterY=-17 CenterZ=0 NormalX=0 NormalY=0 NormalZ=1 AngleXU=0 Radius=2 StartAngle=1.5708 EndAngle=3.14159
    g17: GeomPoint X=15 Y=-15 Z=0
    g18: ArcOfCircle CenterX=18 CenterY=-13 CenterZ=0 NormalX=0 NormalY=0 NormalZ=1 AngleXU=0 Radius=2 StartAngle=4.71239 EndAngle=6.28319
    g19: GeomPoint X=20 Y=-15 Z=0
    g20: ArcOfCircle CenterX=18 CenterY=13 CenterZ=0 NormalX=0 NormalY=0 NormalZ=1 AngleXU=0 Radius=2 StartAngle=0 EndAngle=1.5708
    g21: GeomPoint X=20 Y=15 Z=0
    g22: ArcOfCircle CenterX=17 CenterY=17 CenterZ=0 NormalX=0 NormalY=0 NormalZ=1 AngleXU=0 Radius=2 StartAngle=3.14159 EndAngle=4.71239
    g23: GeomPoint X=15 Y=15 Z=0
    g24: ArcOfCircle CenterX=13 CenterY=18 CenterZ=0 NormalX=0 NormalY=0 NormalZ=1 AngleXU=0 Radius=2 StartAngle=4e-16 EndAngle=1.5708
    g25: GeomPoint X=15 Y=20 Z=0
    g26: ArcOfCircle CenterX=-13 CenterY=18 CenterZ=0 NormalX=0 NormalY=0 NormalZ=1 AngleXU=0 Radius=2 StartAngle=1.5708 EndAngle=3.14159
    g27: GeomPoint X=-15 Y=20 Z=0
    g28: ArcOfCircle CenterX=-17 CenterY=17 CenterZ=0 NormalX=0 NormalY=0 NormalZ=1 AngleXU=0 Radius=2 StartAngle=4.71239 EndAngle=6.28319
    g29: GeomPoint X=-15 Y=15 Z=0
    g30: ArcOfCircle CenterX=-18 CenterY=13 CenterZ=0 NormalX=0 NormalY=0 NormalZ=1 AngleXU=0 Radius=2 StartAngle=1.5708 EndAngle=3.14159
    g31: GeomPoint X=-20 Y=15 Z=0
    g32: ArcOfCircle CenterX=-18 CenterY=-13 CenterZ=0 NormalX=0 NormalY=0 NormalZ=1 AngleXU=0 Radius=2 StartAngle=3.14159 EndAngle=4.71239
    g33: GeomPoint X=-20 Y=-15 Z=0
    g34: ArcOfCircle CenterX=-17 CenterY=-17 CenterZ=0 NormalX=0 NormalY=0 NormalZ=1 AngleXU=0 Radius=2 StartAngle=0 EndAngle=1.5708
    g35: GeomPoint X=-15 Y=-15 Z=0
  constraints (80):
    c: Horizontal(g2)
    c: Vertical(g3)
    c: Symmetric(g21,g31,g-2)
    c: Symmetric(g21,g19,g-1)
    c: DistanceX(g31,g21) = 40
    c: DistanceY(g19,g21) = 30
    c: Horizontal(g4)
    c: Vertical(g7)
    c: Symmetric(g13,g15,g-2)
    c: Symmetric(g15,g25,g-1)
    c: DistanceY(g15,g25) = 40
    c: Vertical(g9)
    c: Vertical(g5)
    c: Vertical(g11)
    c: Horizontal(g10)
    c: Horizontal(g8)
    c: Horizontal(g0)
    c: DistanceX(g13,g15) = 30
    c: DistanceY(g33,g31) = 30
    c: DistanceX(g27,g25) = 30
    c: PointOnObject(g13,g7)
    c: PointOnObject(g13,g6)
    c: Tangent(g7,g12) = 1.5708
    c: Tangent(g6,g12) = 1.5708
    c: Radius(g12) = 2
    c: PointOnObject(g15,g11)
    c: PointOnObject(g15,g6)
    c: Tangent(g11,g14) = 1.5708
    c: Tangent(g6,g14) = 1.5708
    c: PointOnObject(g17,g11)
    c: PointOnObject(g17,g2)
    c: Tangent(g11,g16) = -1.5708
    c: Tangent(g2,g16) = -1.5708
    c: PointOnObject(g19,g2)
    c: PointOnObject(g19,g1)
    c: Tangent(g2,g18) = 1.5708
    c: Tangent(g1,g18) = 1.5708
    c: PointOnObject(g21,g1)
    c: PointOnObject(g21,g8)
    c: Tangent(g1,g20) = 1.5708
    c: Tangent(g8,g20) = 1.5708
    c: PointOnObject(g23,g8)
    c: PointOnObject(g23,g5)
    c: Tangent(g8,g22) = -1.5708
    c: Tangent(g5,g22) = -1.5708
    c: PointOnObject(g25,g5)
    c: PointOnObject(g25,g4)
    c: Tangent(g5,g24) = 1.5708
    c: Tangent(g4,g24) = 1.5708
    c: PointOnObject(g27,g9)
    c: PointOnObject(g27,g4)
    c: Tangent(g9,g26) = 1.5708
    c: Tangent(g4,g26) = 1.5708
    c: PointOnObject(g29,g9)
    c: PointOnObject(g29,g0)
    c: Tangent(g9,g28) = -1.5708
    c: Tangent(g0,g28) = -1.5708
    c: PointOnObject(g31,g0)
    c: PointOnObject(g31,g3)
    c: Tangent(g0,g30) = 1.5708
    c: Tangent(g3,g30) = 1.5708
    c: PointOnObject(g33,g3)
    c: PointOnObject(g33,g10)
    c: Tangent(g3,g32) = 1.5708
    c: Tangent(g10,g32) = 1.5708
    c: PointOnObject(g35,g10)
    c: PointOnObject(g35,g7)
    c: Tangent(g10,g34) = -1.5708
    c: Tangent(g7,g34) = -1.5708
    c: Radius(g34) = 2
    c: Radius(g32) = 2
    c: Radius(g30) = 2
    c: Radius(g28) = 2
    c: Radius(g26) = 2
    c: Radius(g24) = 2
    c: Radius(g22) = 2
    c: Radius(g20) = 2
    c: Radius(g18) = 2
    c: Radius(g16) = 2
    c: Radius(g14) = 2
FEATURE [PartDesign::Pocket] Pocket047
  BaseFeature = -> Pad009
  Direction = (0,0,-1)
  Length = 5
  Length2 = 5
  Profile = -> Sketch056
  ReferenceAxis = -> Sketch056 [N_Axis]
  Type = 1
FEATURE [Sketcher::SketchObject] Sketch057
  ExternalGeometry = -> [Pocket047]
  FullyConstrained = true
  MapMode = 5
  Placement = pos=(25,0,0) rot=(0.57735,0.57735,0.57735;2.0944rad)
  Support = -> [Pocket047]
  sketch-geometry (6):
    g0: LineSegment StartX=-15 StartY=10 StartZ=0 EndX=15 EndY=10 EndZ=0
    g1: LineSegment StartX=20 StartY=5 StartZ=0 EndX=20 EndY=0 EndZ=0
    g2: LineSegment StartX=20 StartY=0 StartZ=0 EndX=-20 EndY=0 EndZ=0
    g3: LineSegment StartX=-20 StartY=0 StartZ=0 EndX=-20 EndY=5 EndZ=0
    g4: ArcOfCircle CenterX=15 CenterY=5 CenterZ=0 NormalX=0 NormalY=0 NormalZ=1 AngleXU=0 Radius=5 StartAngle=1.11001e-11 EndAngle=1.5708
    g5: ArcOfCircle CenterX=-15 CenterY=5 CenterZ=0 NormalX=0 NormalY=0 NormalZ=1 AngleXU=0 Radius=5 StartAngle=1.5708 EndAngle=3.14159
  constraints (15):
    c: Coincident(g1,g2)
    c: Coincident(g2,g3)
    c: Vertical(g1)
    c: Vertical(g3)
    c: PointOnObject(g1,g-1)
    c: Tangent(g1,g4) = 1.5708
    c: Tangent(g0,g4) = 1.5708
    c: Tangent(g0,g5) = 1.5708
    c: Tangent(g3,g5) = 1.5708
    c: Horizontal(g0)
    c: DistanceX(g2,g2) = 40
    c: Symmetric(g2,g1,g-2)
    c: Distance(g-1,g0) = 10
    c: Radius(g5) = 5
    c: Radius(g4) = 5
FEATURE [PartDesign::Pocket] Pocket048
  BaseFeature = -> Pocket047
  Direction = (-1,0,0)
  Length = 5
  Length2 = 5
  Profile = -> Sketch057
  ReferenceAxis = -> Sketch057 [N_Axis]
  Type = 1
FEATURE [Sketcher::SketchObject] Sketch058
  FullyConstrained = true
  MapMode = 5
  Placement = pos=(0,-25,0) rot=(1,0,0;1.5708rad)
  Support = -> [Pocket047]
  sketch-geometry (6):
    g0: LineSegment StartX=-15 StartY=10 StartZ=0 EndX=15 EndY=10 EndZ=0
    g1: LineSegment StartX=20 StartY=5 StartZ=0 EndX=20 EndY=0 EndZ=0
    g2: LineSegment StartX=20 StartY=0 StartZ=0 EndX=-20 EndY=0 EndZ=0
    g3: LineSegment StartX=-20 StartY=0 StartZ=0 EndX=-20 EndY=5 EndZ=0
    g4: ArcOfCircle CenterX=15 CenterY=5 CenterZ=0 NormalX=0 NormalY=0 NormalZ=1 AngleXU=0 Radius=5 StartAngle=1.11e-11 EndAngle=1.5708
    g5: ArcOfCircle CenterX=-15 CenterY=5 CenterZ=0 NormalX=0 NormalY=0 NormalZ=1 AngleXU=0 Radius=5 StartAngle=1.5708 EndAngle=3.14159
  constraints (15):
    c: Coincident(g1,g2)
    c: Coincident(g2,g3)
    c: Horizontal(g0)
    c: Vertical(g1)
    c: Vertical(g3)
    c: Symmetric(g2,g1,g-2)
    c: PointOnObject(g1,g-1)
    c: Tangent(g0,g4) = 1.5708
    c: Tangent(g1,g4) = 1.5708
    c: Tangent(g0,g5) = 1.5708
    c: Tangent(g3,g5) = 1.5708
    c: DistanceX(g2,g2) = 40
    c: Distance(g-1,g0) = 10
    c: Radius(g5) = 5
    c: Radius(g4) = 5
FEATURE [PartDesign::Pocket] Pocket049
  BaseFeature = -> Pocket048
  Direction = (0,1,-2e-16)
  Length = 5
  Length2 = 5
  Profile = -> Sketch058
  ReferenceAxis = -> Sketch058 [N_Axis]
  Type = 1
FEATURE [Sketcher::SketchObject] Sketch059
  FullyConstrained = false
  MapMode = 5
  Placement = pos=(0,0,20) rot=(0,0,1;0rad)
  sketch-geometry (4):
    g0: Circle CenterX=-20 CenterY=20 CenterZ=0 NormalX=0 NormalY=0 NormalZ=1 AngleXU=0 Radius=1.55
    g1: Circle CenterX=20 CenterY=20 CenterZ=0 NormalX=0 NormalY=0 NormalZ=1 AngleXU=0 Radius=1.55
    g2: Circle CenterX=20 CenterY=-20 CenterZ=0 NormalX=0 NormalY=0 NormalZ=1 AngleXU=0 Radius=1.55
    g3: Circle CenterX=-20 CenterY=-20 CenterZ=0 NormalX=0 NormalY=0 NormalZ=1 AngleXU=0 Radius=1.55
  constraints (4):
    c: Diameter(g0) = 3.1
    c: Diameter(g1) = 3.1
    c: Diameter(g2) = 3.1
    c: Diameter(g3) = 3.1
FEATURE [PartDesign::Pocket] Pocket050
  BaseFeature = -> Pocket049
  Direction = (0,0,-1)
  Length = 5
  Length2 = 5
  Profile = -> Sketch059
  ReferenceAxis = -> Sketch059 [N_Axis]
  Type = 0
FEATURE [Sketcher::SketchObject] Sketch060
  ExternalGeometry = -> [Pocket050]
  FullyConstrained = true
  MapMode = 5
  Placement = pos=(0,-25,0) rot=(1,0,0;1.5708rad)
  Support = -> [Pocket050]
  sketch-geometry (2):
    g0: Circle CenterX=-20 CenterY=14 CenterZ=0 NormalX=0 NormalY=0 NormalZ=1 AngleXU=0 Radius=1.4
    g1: Circle CenterX=20 CenterY=14 CenterZ=0 NormalX=0 NormalY=0 NormalZ=1 AngleXU=0 Radius=1.4
  constraints (6):
    c: Diameter(g0) = 2.8
    c: Diameter(g1) = 2.8
    c: Distance(g0,g-5) = 5
    c: Distance(g0,g-3) = 6
    c: Distance(g1,g-3) = 6
    c: Distance(g1,g-4) = 5
FEATURE [PartDesign::Pocket] Pocket051
  BaseFeature = -> Pocket050
  Direction = (0,1,-2e-16)
  Length = 3
  Length2 = 5
  Profile = -> Sketch060
  ReferenceAxis = -> Sketch060 [N_Axis]
  Type = 0
FEATURE [Sketcher::SketchObject] Sketch061
  ExternalGeometry = -> [Pocket051]
  FullyConstrained = true
  MapMode = 5
  Placement = pos=(-25,0,0) rot=(0.57735,-0.57735,-0.57735;2.0944rad)
  Support = -> [Pocket051]
  sketch-geometry (2):
    g0: Circle CenterX=-20 CenterY=14 CenterZ=0 NormalX=0 NormalY=0 NormalZ=1 AngleXU=0 Radius=1.4
    g1: Circle CenterX=20 CenterY=14 CenterZ=0 NormalX=0 NormalY=0 NormalZ=1 AngleXU=0 Radius=1.4
  constraints (6):
    c: Diameter(g0) = 2.8
    c: Diameter(g1) = 2.8
    c: Distance(g0,g-3) = 5
    c: Distance(g0,g-4) = 6
    c: Distance(g1,g-4) = 6
    c: Distance(g1,g-5) = 5
FEATURE [PartDesign::Pocket] Pocket052
  BaseFeature = -> Pocket051
  Direction = (1,0,0)
  Length = 3
  Length2 = 5
  Profile = -> Sketch061
  ReferenceAxis = -> Sketch061 [N_Axis]
  Type = 0
FEATURE [PartDesign::Body] Body010  label="BackplaneBlock008"
  Group = -> [Sketch055,Pad009,Sketch056,Pocket047,Sketch057,Sketch058,Pocket048,Pocket049,Sketch059,Pocket050,Sketch060,Pocket051,Sketch061,Pocket052]
  Origin = -> Origin010
  Placement = pos=(145,145,0) rot=(0,0,1;3.14159rad)
  Tip = -> Pocket052
FEATURE [Part::Box] Box  label="Cube"
  AttacherType = Attacher::AttachEngine3D
  Height = 2
  Length = 10
  Placement = pos=(-10,0,18) rot=(0,0,1;0rad)
  Width = 50
FEATURE [Part::Cylinder] Cylinder
  Angle = 360
  AttacherType = Attacher::AttachEngine3D
  FirstAngle = 0
  Height = 10
  Placement = pos=(-5,12,14) rot=(0,0,1;0rad)
  Radius = 1.55
  SecondAngle = 0
FEATURE [Part::Cylinder] Cylinder001
  Angle = 360
  AttacherType = Attacher::AttachEngine3D
  FirstAngle = 0
  Height = 10
  Placement = pos=(-5,38,14) rot=(0,0,1;0rad)
  Radius = 1.55
  SecondAngle = 0
FEATURE [Part::Cut] Cut
  Base = -> Box
  Tool = -> Cylinder
FEATURE [Part::Cut] Cut001  label="Lip"
  Base = -> Cut
  Tool = -> Cylinder001
FEATURE [App::Link] Link  label="Lip001"
  LinkPlacement = pos=(0,60,0) rot=(0,0,1;0rad)
  LinkedObject = -> Cut001
  Placement = pos=(0,60,0) rot=(0,0,1;0rad)
FEATURE [App::Link] Link019  label="Lip002"
  LinkPlacement = pos=(0,120,0) rot=(0,0,1;0rad)
  LinkedObject = -> Cut001
  Placement = pos=(0,120,0) rot=(0,0,1;0rad)
FEATURE [App::Link] Link020  label="Lip003"
  LinkPlacement = pos=(0,170,0) rot=(0,0,1;4.71239rad)
  LinkedObject = -> Cut001
  Placement = pos=(0,170,0) rot=(0,0,1;4.71239rad)
FEATURE [App::Link] Link021  label="Lip004"
  LinkPlacement = pos=(60,170,0) rot=(0,0,1;4.71239rad)
  LinkedObject = -> Cut001
  Placement = pos=(60,170,0) rot=(0,0,1;4.71239rad)
FEATURE [App::Link] Link022  label="Lip005"
  LinkPlacement = pos=(120,170,0) rot=(0,0,1;4.71239rad)
  LinkedObject = -> Cut001
  Placement = pos=(120,170,0) rot=(0,0,1;4.71239rad)
FEATURE [App::Part] Part
  Group = -> [Body,Link008,Link009,Link010,Link011,Link012,Link013,Link014,Link015,Link016,Link017,Link018,Body002,Body003,Body004,Body005,Body006,Body007,Body008,Body009,Body010,Box,Cylinder,Cylinder001,Cut,Cut001,Link,Link019,Link020,Link021,Link022]
  Origin = -> Origin
FEATURE [Part::MultiFuse] Fusion
  Shapes = -> [Body,Link008,Link009,Link010,Link011,Link012,Link013,Link014,Link015,Link016,Link017,Link018,Body002,Body003,Body004,Body005,Body006,Body007,Body008,Body009,Body010,Cut001,Link,Link019,Link020,Link021,Link022]
FEATURE [Mesh::Feature] Mesh  label="Fusion (Meshed)"
